FCSTD DOCUMENT  (FreeCAD 1.1R38827 (Git))
Label: composit_stand3_basement_assembly
License: All rights reserved
LicenseURL: http://en.wikipedia.org/wiki/All_rights_reserved
objects: App::Link×11, PartDesign::CoordinateSystem×5, App::DocumentObjectGroup×3, App::FeaturePython×1, Spreadsheet::Sheet×1, App::Part×1
note: 5 computed .brp shape members not serialized (recipe doc carries the construction recipe); baked Part::Feature solids carry a one-line shape summary decoded from their .brp
EXTERNAL_REF file=composit_stand3_basement_bottom_model.FCStd obj=Local_CS
EXTERNAL_REF file=composit_stand3_basement_bottom_model.FCStd obj=Body
EXTERNAL_REF file=composit_stand3_basement_amplifier_model.FCStd obj=Local_CS
EXTERNAL_REF file=composit_stand3_basement_bottom_PP_model.FCStd obj=Local_CS001
EXTERNAL_REF file=composit_stand3_basement_amplifier_model.FCStd obj=Body
EXTERNAL_REF file=../bearing_d100.FCStd obj=Local_CS001
EXTERNAL_REF file=composit_stand3_basement_bearing_holder_model.FCStd obj=Local_CS002
EXTERNAL_REF file=composit_stand3_basement_bearing_holder_model.FCStd obj=Body
EXTERNAL_REF file=composit_stand3_basement_amplifier_bearing_holder_model.FCStd obj=Local_CS001
EXTERNAL_REF file=composit_stand3_basement_bearing_holder_model.FCStd obj=Local_CS
EXTERNAL_REF file=composit_stand3_basement_amplifier_bearing_holder_model.FCStd obj=Body
EXTERNAL_REF file=composit_stand3_basement_amplifier_bearing_holder_model.FCStd obj=Local_CS
EXTERNAL_REF file=composit_stand3_basement_top_model.FCStd obj=Local_CS
EXTERNAL_REF file=composit_stand3_basement_top_model.FCStd obj=Body
EXTERNAL_REF file=composit_stand3_basement_top_model.FCStd obj=Local_CS002
EXTERNAL_REF file=../jamb_corner.FCStd obj=Local_CS
EXTERNAL_REF file=../jamb_corner.FCStd obj=Body
EXTERNAL_REF file=composit_stand3_basement_bottom_model.FCStd obj=Local_CS002
EXTERNAL_REF file=../prima_jamb.FCStd obj=Local_CS
EXTERNAL_REF file=../prima_jamb.FCStd obj=Body
EXTERNAL_REF file=composit_stand3_basement_top_PP_model.FCStd obj=Local_CS
EXTERNAL_REF file=composit_stand3_basement_top_model.FCStd obj=Local_CS001
EXTERNAL_REF file=composit_stand3_basement_top_PP_model.FCStd obj=Body
EXTERNAL_REF file=composit_stand3_basement_top_PP_model.FCStd obj=Local_CS001
EXTERNAL_REF file=composit_stand3_basin_holder_model.FCStd obj=Local_CS
EXTERNAL_REF file=composit_stand3_basin_holder_model.FCStd obj=Body
EXTERNAL_REF file=composit_stand3_basement_bottom_PP_model.FCStd obj=Local_CS
EXTERNAL_REF file=composit_stand3_basement_bottom_model.FCStd obj=Local_CS001
EXTERNAL_REF file=composit_stand3_basement_bottom_PP_model.FCStd obj=Body
EXTERNAL_REF file=../bearing_d100.FCStd obj=Local_CS
EXTERNAL_REF file=composit_stand3_basement_amplifier_model.FCStd obj=Local_CS002
EXTERNAL_REF file=../bearing_d100.FCStd obj=Body
EXTERNAL_REF file=composit_stand3_basement_bottom_model.FCStd obj=Local_CS003

FEATURE [App::DocumentObjectGroup] Parts
FEATURE [PartDesign::CoordinateSystem] LCS_Origin
  AttacherType = Attacher::AttachEngine3D
  AttachmentSupport = -> [X_Axis]
  MapMode = 2
FEATURE [App::DocumentObjectGroup] Constraints
FEATURE [App::FeaturePython] Variables  # WARN: FeaturePython — macro-defined, semantics opaque (R4)
  Type = App::PropertyContainer
FEATURE [App::DocumentObjectGroup] Configurations
FEATURE [App::Link] bottom
  AttachedBy = #Local_CS
  AttachedTo = Parent Assembly#LCS_Origin
  LinkedObject = -> <external composit_stand3_basement_bottom_model.FCStd>#Body
  SolverId = Asm4EE
  expr: Placement = LCS_Origin.Placement * AttachmentOffset * composit_stand3_basement_bottom_model#Local_CS.Placement ^ -1
FEATURE [App::Link] amplifier
  AttachedBy = #Local_CS
  AttachedTo = bottom_PP#Local_CS001
  LinkPlacement = pos=(0,0,21) rot=(0,0,1;0rad)
  LinkedObject = -> <external composit_stand3_basement_amplifier_model.FCStd>#Body
  Placement = pos=(0,0,21) rot=(0,0,1;0rad)
  SolverId = Asm4EE
  expr: Placement = bottom_PP.Placement * composit_stand3_basement_bottom_PP_model#Local_CS001.Placement * AttachmentOffset * composit_stand3_basement_amplifier_model#Local_CS.Placement ^ -1
FEATURE [App::Link] bearing_holder
  AttachedBy = #Local_CS002
  AttachedTo = bearing_d100#Local_CS001
  AttachmentOffset = pos=(0,0,0) rot=(1,0,0;3.14159rad)
  LinkPlacement = pos=(0,2e-15,72) rot=(1,0,0;3.14159rad)
  LinkedObject = -> <external composit_stand3_basement_bearing_holder_model.FCStd>#Body
  Placement = pos=(0,2e-15,72) rot=(1,0,0;3.14159rad)
  SolverId = Asm4EE
  expr: Placement = bearing_d100.Placement * bearing_d100#Local_CS001.Placement * AttachmentOffset * composit_stand3_basement_bearing_holder_model#Local_CS002.Placement ^ -1
FEATURE [App::Link] amplifier_bearing_holder
  AttachedBy = #Local_CS001
  AttachedTo = bearing_holder#Local_CS
  LinkPlacement = pos=(0,4.2e-15,90) rot=(1,0,0;3.14159rad)
  LinkedObject = -> <external composit_stand3_basement_amplifier_bearing_holder_model.FCStd>#Body
  Placement = pos=(0,4.2e-15,90) rot=(1,0,0;3.14159rad)
  SolverId = Asm4EE
  expr: Placement = bearing_holder.Placement * composit_stand3_basement_bearing_holder_model#Local_CS.Placement * AttachmentOffset * composit_stand3_basement_amplifier_bearing_holder_model#Local_CS001.Placement ^ -1
FEATURE [App::Link] top
  AttachedBy = #Local_CS
  AttachedTo = amplifier_bearing_holder#Local_CS
  AttachmentOffset = pos=(0,0,0) rot=(1,0,0;3.14159rad)
  LinkPlacement = pos=(0,4.2e-15,90) rot=(0,0,1;0rad)
  LinkedObject = -> <external composit_stand3_basement_top_model.FCStd>#Body
  Placement = pos=(0,4.2e-15,90) rot=(0,0,1;0rad)
  SolverId = Asm4EE
  expr: Placement = amplifier_bearing_holder.Placement * composit_stand3_basement_amplifier_bearing_holder_model#Local_CS.Placement * AttachmentOffset * composit_stand3_basement_top_model#Local_CS.Placement ^ -1
FEATURE [App::Link] jamb_corner
  AttachedBy = #Local_CS
  AttachedTo = top#Local_CS002
  LinkPlacement = pos=(215,-2.1,90) rot=(-0.57735,-0.57735,0.57735;2.0944rad)
  LinkedObject = -> <external ../jamb_corner.FCStd>#Body
  Placement = pos=(215,-2.1,90) rot=(-0.57735,-0.57735,0.57735;2.0944rad)
  SolverId = Asm4EE
  expr: Placement = top.Placement * composit_stand3_basement_top_model#Local_CS002.Placement * AttachmentOffset * jamb_corner#Local_CS.Placement ^ -1
FEATURE [App::Link] prima_jamb
  AttachedBy = #Local_CS
  AttachedTo = bottom#Local_CS002
  LinkPlacement = pos=(215,0,21) rot=(0,0,1;0rad)
  LinkedObject = -> <external ../prima_jamb.FCStd>#Body
  Placement = pos=(215,0,21) rot=(0,0,1;0rad)
  SolverId = Asm4EE
  expr: Placement = bottom.Placement * composit_stand3_basement_bottom_model#Local_CS002.Placement * AttachmentOffset * prima_jamb#Local_CS.Placement ^ -1
FEATURE [App::Link] top_PP
  AttachedBy = #Local_CS
  AttachedTo = top#Local_CS001
  LinkPlacement = pos=(0,8.6e-15,108) rot=(0,0,1;0rad)
  LinkedObject = -> <external composit_stand3_basement_top_PP_model.FCStd>#Body
  Placement = pos=(0,8.6e-15,108) rot=(0,0,1;0rad)
  SolverId = Asm4EE
  expr: Placement = top.Placement * composit_stand3_basement_top_model#Local_CS001.Placement * AttachmentOffset * composit_stand3_basement_top_PP_model#Local_CS.Placement ^ -1
FEATURE [App::Link] basin_holder
  AttachedBy = #Local_CS
  AttachedTo = top_PP#Local_CS001
  LinkPlacement = pos=(0,9.3e-15,111) rot=(0,0,1;0rad)
  LinkedObject = -> <external composit_stand3_basin_holder_model.FCStd>#Body
  Placement = pos=(0,9.3e-15,111) rot=(0,0,1;0rad)
  SolverId = Asm4EE
  expr: Placement = top_PP.Placement * composit_stand3_basement_top_PP_model#Local_CS001.Placement * AttachmentOffset * composit_stand3_basin_holder_model#Local_CS.Placement ^ -1
FEATURE [App::Link] bottom_PP
  AttachedBy = #Local_CS
  AttachedTo = bottom#Local_CS001
  LinkPlacement = pos=(0,0,18) rot=(0,0,1;0rad)
  LinkedObject = -> <external composit_stand3_basement_bottom_PP_model.FCStd>#Body
  Placement = pos=(0,0,18) rot=(0,0,1;0rad)
  SolverId = Asm4EE
  expr: Placement = bottom.Placement * composit_stand3_basement_bottom_model#Local_CS001.Placement * AttachmentOffset * composit_stand3_basement_bottom_PP_model#Local_CS.Placement ^ -1
FEATURE [PartDesign::CoordinateSystem] top_LCS
  AttacherType = Attacher::AttachEngine3D
  AttachmentSupport = -> [top_PP]
  Placement = pos=(0,0,111) rot=(0,0,1;0rad)
FEATURE [App::Link] bearing_d100
  AttachedBy = #Local_CS
  AttachedTo = amplifier#Local_CS002
  LinkPlacement = pos=(0,0,37) rot=(0,0,1;0rad)
  LinkedObject = -> <external ../bearing_d100.FCStd>#Body
  Placement = pos=(0,0,37) rot=(0,0,1;0rad)
  SolverId = Asm4EE
  expr: Placement = amplifier.Placement * composit_stand3_basement_amplifier_model#Local_CS002.Placement * AttachmentOffset * bearing_d100#Local_CS.Placement ^ -1
FEATURE [Spreadsheet::Sheet] Spreadsheet  label="Properties"
  cells = B2(total_height)==111 mm
FEATURE [PartDesign::CoordinateSystem] bar1_LCS
  AttacherType = Attacher::AttachEngine3D
  AttachmentOffset = pos=(383.5,0,21) rot=(0,0,1;3.14159rad)
  AttachmentSupport = -> [LCS_Origin]
  MapMode = 5
  Placement = pos=(383.5,0,21) rot=(0,0,1;3.14159rad)
  expr: AttachmentOffset = <<bottom>>.Placement * <<composit_stand3_basement_bottom_model>>#<<bar_LCS>>.Placement
FEATURE [PartDesign::CoordinateSystem] bar2_LCS
  AttacherType = Attacher::AttachEngine3D
  AttachmentOffset = pos=(-191.75,332.121,21) rot=(0,0,1;5.23599rad)
  AttachmentSupport = -> [LCS_Origin]
  MapMode = 5
  Placement = pos=(-191.75,332.121,21) rot=(0,0,1;5.23599rad)
  expr: AttachmentOffset = placement(vector(0; 0; 0); rotation(120 deg; 0; 0)) * <<bottom>>.Placement * <<composit_stand3_basement_bottom_model>>#<<bar_LCS>>.Placement
FEATURE [PartDesign::CoordinateSystem] bar3_LCS
  AttacherType = Attacher::AttachEngine3D
  AttachmentOffset = pos=(-191.75,-332.121,21) rot=(0,0,-1;5.23599rad)
  AttachmentSupport = -> [LCS_Origin]
  MapMode = 5
  Placement = pos=(-191.75,-332.121,21) rot=(0,0,-1;5.23599rad)
  expr: AttachmentOffset = placement(vector(0; 0; 0); rotation(240 deg; 0; 0)) * <<bottom>>.Placement * <<composit_stand3_basement_bottom_model>>#<<bar_LCS>>.Placement
FEATURE [App::Part] Assembly  label="basement_Assembly"
  AssemblyType = Part::Link
  Group = -> [LCS_Origin,Constraints,Variables,Configurations,bottom,amplifier,bearing_holder,amplifier_bearing_holder,top,jamb_corner,prima_jamb,top_PP,basin_holder,bottom_PP,top_LCS,bearing_d100,bar1_LCS,bar2_LCS,bar3_LCS]
  Origin = -> Origin
  Type = Assembly

RESOLVED EXTERNAL PARTS (link-assembly join: the EXTERNAL_REF files above that resolve inside this repo's crawl, each included once):
---- part ../bearing_d100.FCStd = doc fcstd_fc5883dd0358 ----
FCSTD DOCUMENT  (FreeCAD 1.1R38827 (Git))
Label: bearing_d100
License: All rights reserved
LicenseURL: http://en.wikipedia.org/wiki/All_rights_reserved
objects: PartDesign::CoordinateSystem×2, Sketcher::SketchObject×1, PartDesign::SubShapeBinder×1, PartDesign::Revolution×1, PartDesign::Body×1
note: 9 computed .brp shape members not serialized (recipe doc carries the construction recipe); baked Part::Feature solids carry a one-line shape summary decoded from their .brp

FEATURE [Sketcher::SketchObject] Sketch  label="main_Sketch"
  ArcFitTolerance = 0
  FullyConstrained = true
  MakeInternals = false
  Placement = pos=(0,0,0) rot=(1,0,0;1.5708rad)
  sketch-geometry (4):
    g0: LineSegment StartX=37.5 StartY=0 StartZ=0 EndX=50 EndY=0 EndZ=0
    g1: LineSegment StartX=50 StartY=0 StartZ=0 EndX=50 EndY=19 EndZ=0
    g2: LineSegment StartX=50 StartY=19 StartZ=0 EndX=37.5 EndY=19 EndZ=0
    g3: LineSegment StartX=37.5 StartY=19 StartZ=0 EndX=37.5 EndY=0 EndZ=0
  constraints (12):
    c: Coincident(g0,g1)
    c: Coincident(g1,g2)
    c: Coincident(g2,g3)
    c: Coincident(g3,g0)
    c: Horizontal(g0)
    c: Horizontal(g2)
    c: Vertical(g1)
    c: Vertical(g3)
    c: PointOnObject(g0,g-1)
    c: DistanceX(g0) = 37.5  'min_r'
    c: DistanceX(g0) = 50  'max_r'
    c: DistanceY(g3,g3) = 19  'height'
FEATURE [PartDesign::SubShapeBinder] Binder
  BindCopyOnChange = 0
  BindMode = 0
  ClaimChildren = true
  Context = -> Body [Binder.]
  Fuse = false
  MakeFace = true
  OffsetFill = false
  OffsetIntersection = false
  OffsetJoinType = 0
  OffsetOpenResult = false
  PartialLoad = false
  Placement = pos=(0,0,0) rot=(1,0,0;1.5708rad)
  Relative = false
  Support = -> [Sketch]
  _Version = 2
  expr: Placement = Support[0][0].Placement
FEATURE [PartDesign::Revolution] Revolution
  Angle = 360
  Angle2 = 60
  Axis = (1e-16,1e-16,1)
  Base = (0,0,0)
  Placement = pos=(0,0,0) rot=(1,0,0;1.5708rad)
  Profile = -> Binder [Face1]
  ReferenceAxis = -> Z_Axis
  Reversed = true
  Suppressed = false
  Type = 0
FEATURE [PartDesign::CoordinateSystem] Local_CS  label="bottom_LCS"
  AttacherType = Attacher::AttachEngine3D
  AttachmentSupport = -> [XY_Plane]
  MapMode = 5
FEATURE [PartDesign::CoordinateSystem] Local_CS001  label="top_LCS"
  AttacherType = Attacher::AttachEngine3D
  AttachmentOffset = pos=(0,0,19) rot=(0,0,1;0rad)
  AttachmentSupport = -> [XY_Plane]
  MapMode = 5
  Placement = pos=(0,0,19) rot=(0,0,1;0rad)
  expr: .AttachmentOffset.Base.z = <<main_Sketch>>.Constraints.height
FEATURE [PartDesign::Body] Body  label="bearing_d100"
  AllowCompound = false
  Group = -> [Binder,Revolution,Local_CS,Local_CS001]
  Origin = -> Origin
  Tip = -> Revolution
---- part ../jamb_corner.FCStd = doc fcstd_c531c7f2f68e ----
FCSTD DOCUMENT  (FreeCAD 1.1R38827 (Git))
Label: jamb_corner
License: All rights reserved
LicenseURL: http://en.wikipedia.org/wiki/All_rights_reserved
objects: Part::FeaturePython×5, PartDesign::Body×2, Sketcher::SketchObject×1, PartDesign::FeaturePython×1, Part::Cylinder×1, Part::MultiFuse×1, PartDesign::Boolean×1, PartDesign::CoordinateSystem×1
note: 16 computed .brp shape members not serialized (recipe doc carries the construction recipe); baked Part::Feature solids carry a one-line shape summary decoded from their .brp

FEATURE [Sketcher::SketchObject] Sketch
  ArcFitTolerance = 0
  FullyConstrained = true
  MakeInternals = false
  sketch-geometry (2):
    g0: LineSegment StartX=0 StartY=61.5 StartZ=0 EndX=0 EndY=0 EndZ=0
    g1: LineSegment StartX=0 StartY=0 StartZ=0 EndX=102 EndY=0 EndZ=0
  constraints (6):
    c: PointOnObject(g0,g-2)
    c: Coincident(g0,g-1)
    c: Coincident(g0,g1)
    c: PointOnObject(g1,g-1)
    c: DistanceX(g1) = 102
    c: DistanceY(g0) = 61.5
FEATURE [Part::FeaturePython] Placment  # WARN: FeaturePython — macro-defined, semantics opaque (R4)
  AttacherType = Attacher::AttachEngine3D
  ExposePlacement = true
  MarkerShape = 1
  MarkerSize = 50
  NumElements = 1
  Placement = pos=(43.5,0,0) rot=(1,0,0;0rad)
  Type = lattice2AttachablePlacement.AttachablePlacement
  isLattice = 1
FEATURE [Part::FeaturePython] Placment001  # WARN: FeaturePython — macro-defined, semantics opaque (R4)
  AttacherType = Attacher::AttachEngine3D
  ExposePlacement = true
  MarkerShape = 1
  MarkerSize = 50
  NumElements = 1
  Placement = pos=(68.5,0,0) rot=(1,0,0;0rad)
  Type = lattice2AttachablePlacement.AttachablePlacement
  isLattice = 1
FEATURE [Part::FeaturePython] Placment002  # WARN: FeaturePython — macro-defined, semantics opaque (R4)
  AttacherType = Attacher::AttachEngine3D
  ExposePlacement = true
  MarkerShape = 1
  MarkerSize = 50
  NumElements = 1
  Placement = pos=(91,0,0) rot=(1,0,0;0rad)
  Type = lattice2AttachablePlacement.AttachablePlacement
  isLattice = 1
FEATURE [PartDesign::FeaturePython] BaseBend  # WARN: FeaturePython — macro-defined, semantics opaque (R4)
  BendSide = 1
  BendSketch = -> Sketch
  MidPlane = true
  Reverse = false
  Suppressed = false
  length = 20
  radius = 6
  thickness = 4.3
FEATURE [Part::Cylinder] Cylinder
  Angle = 360
  AttacherType = Attacher::AttachEngine3D
  FirstAngle = 0
  Height = 10
  Placement = pos=(0,0,0) rot=(1,0,0;3.14159rad)
  Radius = 2
  SecondAngle = 0
FEATURE [Part::FeaturePython] Join  label="holes_hor"  # WARN: FeaturePython — macro-defined, semantics opaque (R4)
  ExposePlacement = false
  Interleave = false
  Links = -> [Placment,Placment001,Placment002]
  MarkerShape = 1
  MarkerSize = 0
  NumElements = 3
  Placement = pos=(0,0,0) rot=(1,0,0;1.5708rad)
  Type = lattice2JoinArrays.JoinArrays
  isLattice = 1
FEATURE [Part::FeaturePython] Populate  label="Populate holes_hor with Cylinder"  # WARN: FeaturePython — macro-defined, semantics opaque (R4)
  Copying = 0
  ExposePlacement = false
  MarkerShape = 1
  MarkerSize = 0
  NumElements = 0
  Object = -> Cylinder
  OutputCompounding = 1
  PlacementsTo = -> Join
  Referencing = 0
  Type = lattice2PopulateCopies.LatticePopulateCopies
  isLattice = 0
FEATURE [PartDesign::Body] Body001
  AllowCompound = false
  Origin = -> Origin001
FEATURE [Part::MultiFuse] Fusion
  Shapes = -> [Populate]
FEATURE [PartDesign::Boolean] Boolean
  BaseFeature = -> BaseBend
  Group = -> [Fusion]
  Suppressed = false
  Type = 1
  UsePlacement = true
FEATURE [PartDesign::CoordinateSystem] Local_CS  label="base_LCS"
  AttacherType = Attacher::AttachEngine3D
  AttachmentSupport = -> [YZ_Plane]
  MapMode = 5
  Placement = pos=(0,0,0) rot=(0.57735,0.57735,0.57735;2.0944rad)
FEATURE [PartDesign::Body] Body  label="jamb_corner"
  AllowCompound = false
  Group = -> [BaseBend,Boolean,Local_CS]
  Origin = -> Origin
  Tip = -> Boolean
---- part ../prima_jamb.FCStd = doc fcstd_baa8a8553cea ----
FCSTD DOCUMENT  (FreeCAD 1.1R38827 (Git))
Label: prima_jamb
License: All rights reserved
LicenseURL: http://en.wikipedia.org/wiki/All_rights_reserved
objects: Sketcher::SketchObject×1, PartDesign::Revolution×1, Part::Cylinder×1, Part::Compound×1, PartDesign::Boolean×1, PartDesign::CoordinateSystem×1, PartDesign::Body×1
note: 11 computed .brp shape members not serialized (recipe doc carries the construction recipe); baked Part::Feature solids carry a one-line shape summary decoded from their .brp

FEATURE [Sketcher::SketchObject] Sketch
  ArcFitTolerance = 0
  AttachmentSupport = -> [XZ_Plane]
  FullyConstrained = true
  MakeInternals = false
  MapMode = 5
  Placement = pos=(0,0,0) rot=(1,0,0;1.5708rad)
  sketch-geometry (6):
    g0: LineSegment StartX=0 StartY=0 StartZ=0 EndX=20.75 EndY=0 EndZ=0
    g1: LineSegment StartX=20.75 StartY=0 StartZ=0 EndX=20.75 EndY=48.0542 EndZ=0
    g2: ArcOfCircle CenterX=18.1 CenterY=40.4 CenterZ=0 NormalX=0 NormalY=0 NormalZ=1 AngleXU=0 Radius=8.1 StartAngle=1.2375 EndAngle=3.14159
    g3: LineSegment StartX=0 StartY=0 StartZ=0 EndX=0 EndY=40.4 EndZ=0
    g4: LineSegment StartX=0 StartY=40.4 StartZ=0 EndX=10 EndY=40.4 EndZ=0
    g5: LineSegment [constr] StartX=0 StartY=48.5 StartZ=0 EndX=18.1 EndY=48.5 EndZ=0
  constraints (18):
    c: Coincident(g-1,g0)
    c: PointOnObject(g0,g-1)
    c: Coincident(g0,g1)
    c: Vertical(g1)
    c: Coincident(g0,g3)
    c: PointOnObject(g3,g-2)
    c: Coincident(g3,g4)
    c: Coincident(g4,g2)
    c: Horizontal(g4)
    c: DistanceX(g0) = 20.75
    c: Perpendicular(g2,g4)
    c: DistanceX(g2) = 10
    c: Tangent(g5,g2) = 1.5708
    c: Horizontal(g5)
    c: PointOnObject(g5,g-2)
    c: DistanceY(g3,g5) = 8.1
    c: Coincident(g1,g2)
    c: DistanceY(g5) = 48.5
FEATURE [PartDesign::Revolution] Revolution
  Angle = 360
  Angle2 = 60
  Axis = (0,2e-16,1)
  Base = (0,0,0)
  Placement = pos=(0,0,0) rot=(1,0,0;1.5708rad)
  Profile = -> Sketch
  ReferenceAxis = -> Sketch [V_Axis]
  Reversed = true
  Suppressed = false
  Type = 0
FEATURE [Part::Cylinder] Cylinder
  Angle = 360
  AttacherType = Attacher::AttachEngine3D
  FirstAngle = 0
  Height = 50
  Radius = 3.5
  SecondAngle = 0
FEATURE [Part::Compound] Compound
  Links = -> [Cylinder]
FEATURE [PartDesign::Boolean] Boolean
  BaseFeature = -> Revolution
  Group = -> [Compound]
  Suppressed = false
  Type = 1
  UsePlacement = true
FEATURE [PartDesign::CoordinateSystem] Local_CS
  AttacherType = Attacher::AttachEngine3D
  AttachmentSupport = -> [XY_Plane]
  MapMode = 5
FEATURE [PartDesign::Body] Body  label="prima_jamb"
  AllowCompound = false
  Group = -> [Sketch,Revolution,Boolean,Local_CS]
  Origin = -> Origin
  Tip = -> Boolean
---- part composit_stand3_basement_amplifier_bearing_holder_model.FCStd = doc fcstd_344d85539f5e ----
FCSTD DOCUMENT  (FreeCAD 1.1R38827 (Git))
Label: composit_stand3_basement_amplifier_bearing_holder_model
License: All rights reserved
LicenseURL: http://en.wikipedia.org/wiki/All_rights_reserved
objects: Part::FeaturePython×5, PartDesign::SubShapeBinder×2, PartDesign::Pad×2, App::Link×2, PartDesign::Body×2, PartDesign::CoordinateSystem×2, Part::Mirroring×1, Part::Compound×1, Part::Cylinder×1, Sketcher::SketchObject×1, Part::MultiFuse×1, PartDesign::Boolean×1
note: 25 computed .brp shape members not serialized (recipe doc carries the construction recipe); baked Part::Feature solids carry a one-line shape summary decoded from their .brp
EXTERNAL_REF file=composit_stand3_basement_amplifier_main.FCStd obj=Sketch
EXTERNAL_REF file=composit_stand3_basement_amplifier_main.FCStd obj=Join001
EXTERNAL_REF file=composit_stand3_basement_amplifier_main.FCStd obj=Cylinder

FEATURE [PartDesign::SubShapeBinder] Binder
  BindCopyOnChange = 0
  BindMode = 0
  ClaimChildren = true
  Fuse = false
  MakeFace = true
  OffsetFill = false
  OffsetIntersection = false
  OffsetJoinType = 0
  OffsetOpenResult = false
  PartialLoad = false
  Relative = true
  Support = -> [<external composit_stand3_basement_amplifier_main.FCStd>#Sketch]
  _Version = 2
FEATURE [Part::Mirroring] Part__Mirroring  label="Binder (Mirror #1)"
  Base = (0,0,0)
  Normal = (0,1,0)
  Source = -> Binder
FEATURE [Part::FeaturePython] PolarArray  # WARN: FeaturePython — macro-defined, semantics opaque (R4)
  Alignment = 0
  AttacherType = Attacher::AttachEngine3D
  CellStart = A1
  Count = 3
  DistributionLaw = 0
  EndInclusive = false
  ExposePlacement = false
  FlipX = false
  FlipZ = false
  GeneratorMode = 0
  MarkerShape = 1
  MarkerSize = 0
  NumElements = 3
  OrientMode = 2
  Radius = 100
  Reverse = false
  SpanEnd = 360
  SpanStart = 0
  Step = 120
  Type = lattice2PolarArray2.PolarArray
  UseArcRadius = false
  UseArcRange = 0
  VSGVersion = 1
  Values = 0.0 | 120.0 | 240.0
  ValuesSource = 2
  isLattice = 1
FEATURE [Part::Compound] Compound
  Links = -> [Binder,Part__Mirroring]
FEATURE [Part::FeaturePython] Populate  label="Populate PolarArray with Compound"  # WARN: FeaturePython — macro-defined, semantics opaque (R4)
  Copying = 0
  ExposePlacement = false
  MarkerShape = 1
  MarkerSize = 0
  NumElements = 0
  Object = -> Compound
  OutputCompounding = 1
  PlacementsTo = -> PolarArray
  Referencing = 1
  Type = lattice2PopulateCopies.LatticePopulateCopies
  isLattice = 0
FEATURE [Part::FeaturePython] Connect  # WARN: FeaturePython — macro-defined, semantics opaque (R4)
  Objects = -> [Populate]
  Tolerance = 0
FEATURE [PartDesign::SubShapeBinder] Binder001
  BindCopyOnChange = 0
  BindMode = 0
  ClaimChildren = true
  Context = -> Body [Binder001.]
  Fuse = false
  MakeFace = false
  OffsetFill = false
  OffsetIntersection = false
  OffsetJoinType = 0
  OffsetOpenResult = false
  PartialLoad = false
  Relative = true
  Support = -> [Connect]
  _Version = 2
FEATURE [PartDesign::Pad] Pad
  Direction = (0,0,1)
  Length = 18
  Length2 = 10
  Profile = -> Binder001
  Refine = true
  Suppressed = false
  Type = 0
FEATURE [App::Link] Link  label="Populate PolarArray with Join"
  LinkedObject = -> <external composit_stand3_basement_amplifier_main.FCStd>#Join001
FEATURE [Part::Cylinder] Cylinder  label="hole_5,2_mm"
  Angle = 360
  AttacherType = Attacher::AttachEngine3D
  FirstAngle = 0
  Height = 18
  Radius = 2.6
  SecondAngle = 0
FEATURE [Part::FeaturePython] Join  label="holes_placements"  # WARN: FeaturePython — macro-defined, semantics opaque (R4)
  ExposePlacement = false
  Interleave = false
  Links = -> [Link]
  MarkerShape = 1
  MarkerSize = 0
  NumElements = 14
  Type = lattice2JoinArrays.JoinArrays
  isLattice = 1
FEATURE [Part::FeaturePython] Populate001  label="Populate Populate PolarArray with Join with hole_5_mm"  # WARN: FeaturePython — macro-defined, semantics opaque (R4)
  Copying = 0
  ExposePlacement = false
  MarkerShape = 1
  MarkerSize = 0
  NumElements = 0
  Object = -> Cylinder
  OutputCompounding = 1
  PlacementsTo = -> Join
  Referencing = 0
  Type = lattice2PopulateCopies.LatticePopulateCopies
  isLattice = 0
FEATURE [App::Link] Link003  label="axis_bolt"
  LinkedObject = -> <external composit_stand3_basement_amplifier_main.FCStd>#Cylinder
FEATURE [Sketcher::SketchObject] Sketch
  ArcFitTolerance = 0
  AttachmentSupport = -> [XY_Plane002]
  FullyConstrained = true
  MakeInternals = false
  MapMode = 5
  sketch-geometry (7):
    g0: LineSegment StartX=11.0274 StartY=0 StartZ=0 EndX=5.5137 EndY=9.55 EndZ=0
    g1: LineSegment StartX=5.5137 StartY=9.55 StartZ=0 EndX=-5.5137 EndY=9.55 EndZ=0
    g2: LineSegment StartX=-5.5137 StartY=9.55 StartZ=0 EndX=-11.0274 EndY=0 EndZ=0
    g3: LineSegment StartX=-11.0274 StartY=1e-16 StartZ=0 EndX=-5.5137 EndY=-9.55 EndZ=0
    g4: LineSegment StartX=-5.5137 StartY=-9.55 StartZ=0 EndX=5.5137 EndY=-9.55 EndZ=0
    g5: LineSegment StartX=5.5137 StartY=-9.55 StartZ=0 EndX=11.0274 EndY=0 EndZ=0
    g6: Circle [constr] CenterX=0 CenterY=0 CenterZ=0 NormalX=0 NormalY=0 NormalZ=1 AngleXU=0 Radius=11.0274
  constraints (16):
    c: Coincident(g0,g1)
    c: Coincident(g1,g2)
    c: Coincident(g2,g3)
    c: Coincident(g3,g4)
    c: Coincident(g4,g5)
    c: Coincident(g5,g0)
    c: Equal(g0, g1-g5) x5
    c: PointOnObject(g0,g6)
    c: PointOnObject(g1,g6)
    c: PointOnObject(g2,g6)
    c: PointOnObject(g3,g6)
    c: PointOnObject(g4,g6)
    c: PointOnObject(g5,g6)
    c: Coincident(g6,g-1)
    c: PointOnObject(g5,g-1)
    c: DistanceY(g4,g0) = 19.1
FEATURE [PartDesign::Pad] Pad001
  Direction = (0,0,1)
  Length = 7.4
  Length2 = 10
  Profile = -> Sketch
  ReferenceAxis = -> Sketch [N_Axis]
  Suppressed = false
  Type = 0
FEATURE [PartDesign::Body] Body002  label="Body003"
  AllowCompound = false
  Group = -> [Sketch,Pad001]
  Origin = -> Origin002
  Tip = -> Pad001
FEATURE [Part::MultiFuse] Fusion
  Shapes = -> [Populate001,Link003,Body002]
FEATURE [PartDesign::Boolean] Boolean
  BaseFeature = -> Pad
  Group = -> [Fusion]
  Suppressed = false
  Type = 1
  UsePlacement = true
FEATURE [PartDesign::CoordinateSystem] Local_CS  label="bottom_LCS"
  AttacherType = Attacher::AttachEngine3D
  AttachmentSupport = -> [XY_Plane]
  MapMode = 5
FEATURE [PartDesign::CoordinateSystem] Local_CS001  label="top_LCS"
  AttacherType = Attacher::AttachEngine3D
  AttachmentOffset = pos=(0,0,18) rot=(0,0,1;0rad)
  AttachmentSupport = -> [XY_Plane]
  MapMode = 5
  Placement = pos=(0,0,18) rot=(0,0,1;0rad)
FEATURE [PartDesign::Body] Body  label="amplifier_bearing_holder"
  AllowCompound = false
  Group = -> [Binder001,Pad,Boolean,Local_CS,Local_CS001]
  Origin = -> Origin
  Tip = -> Boolean
---- part composit_stand3_basement_amplifier_model.FCStd = doc fcstd_fba40b1622f7 ----
FCSTD DOCUMENT  (FreeCAD 1.1R38827 (Git))
Label: composit_stand3_basement_amplifier_model
License: All rights reserved
LicenseURL: http://en.wikipedia.org/wiki/All_rights_reserved
objects: Part::FeaturePython×6, App::Link×5, PartDesign::CoordinateSystem×3, PartDesign::SubShapeBinder×2, Part::Mirroring×1, Part::Compound×1, PartDesign::Pad×1, Part::Cylinder×1, Part::MultiFuse×1, PartDesign::Boolean×1, PartDesign::Body×1
note: 21 computed .brp shape members not serialized (recipe doc carries the construction recipe); baked Part::Feature solids carry a one-line shape summary decoded from their .brp
EXTERNAL_REF file=composit_stand3_basement_amplifier_main.FCStd obj=Sketch
EXTERNAL_REF file=composit_stand3_basement_amplifier_main.FCStd obj=Join001
EXTERNAL_REF file=composit_stand3_basement_amplifier_main.FCStd obj=Cylinder
EXTERNAL_REF file=composit_stand3_basement_bearing_holder_main.FCStd obj=Placment
EXTERNAL_REF file=../bearing_d100.FCStd obj=Body
EXTERNAL_REF file=composit_stand3_basement_amplifier_main.FCStd obj=Body

FEATURE [PartDesign::SubShapeBinder] Binder
  BindCopyOnChange = 0
  BindMode = 0
  ClaimChildren = false
  Fuse = false
  MakeFace = true
  OffsetFill = false
  OffsetIntersection = false
  OffsetJoinType = 0
  OffsetOpenResult = false
  PartialLoad = false
  Relative = true
  Support = -> [<external composit_stand3_basement_amplifier_main.FCStd>#Sketch]
  _Version = 2
FEATURE [Part::Mirroring] Part__Mirroring  label="Binder (Mirror #1)"
  Base = (0,0,0)
  Normal = (0,1,0)
  Source = -> Binder
FEATURE [Part::FeaturePython] PolarArray  # WARN: FeaturePython — macro-defined, semantics opaque (R4)
  Alignment = 0
  AttacherType = Attacher::AttachEngine3D
  CellStart = A1
  Count = 3
  DistributionLaw = 0
  EndInclusive = false
  ExposePlacement = false
  FlipX = false
  FlipZ = false
  GeneratorMode = 0
  MarkerShape = 1
  MarkerSize = 0
  NumElements = 3
  OrientMode = 2
  Radius = 100
  Reverse = false
  SpanEnd = 360
  SpanStart = 0
  Step = 120
  Type = lattice2PolarArray2.PolarArray
  UseArcRadius = false
  UseArcRange = 0
  VSGVersion = 1
  Values = 0.0 | 120.0 | 240.0
  ValuesSource = 2
  isLattice = 1
FEATURE [Part::Compound] Compound
  Links = -> [Binder,Part__Mirroring]
FEATURE [Part::FeaturePython] Populate  label="Populate PolarArray with Compound"  # WARN: FeaturePython — macro-defined, semantics opaque (R4)
  Copying = 0
  ExposePlacement = false
  MarkerShape = 1
  MarkerSize = 0
  NumElements = 0
  Object = -> Compound
  OutputCompounding = 1
  PlacementsTo = -> PolarArray
  Referencing = 1
  Type = lattice2PopulateCopies.LatticePopulateCopies
  isLattice = 0
FEATURE [Part::FeaturePython] Connect  # WARN: FeaturePython — macro-defined, semantics opaque (R4)
  Objects = -> [Populate]
  Tolerance = 0
FEATURE [PartDesign::SubShapeBinder] Binder001
  BindCopyOnChange = 0
  BindMode = 0
  ClaimChildren = true
  Context = -> Body [Binder001.]
  Fuse = false
  MakeFace = false
  OffsetFill = false
  OffsetIntersection = false
  OffsetJoinType = 0
  OffsetOpenResult = false
  PartialLoad = false
  Relative = true
  Support = -> [Connect]
  _Version = 2
FEATURE [PartDesign::Pad] Pad
  Direction = (0,0,1)
  Length = 18
  Length2 = 10
  Profile = -> Binder001
  Refine = true
  Suppressed = false
  Type = 0
FEATURE [App::Link] Link  label="Populate PolarArray with Join"
  LinkedObject = -> <external composit_stand3_basement_amplifier_main.FCStd>#Join001
FEATURE [Part::Cylinder] Cylinder  label="hole_5,2_mm"
  Angle = 360
  AttacherType = Attacher::AttachEngine3D
  FirstAngle = 0
  Height = 18
  Radius = 2.6
  SecondAngle = 0
FEATURE [Part::FeaturePython] Join  label="holes_placements"  # WARN: FeaturePython — macro-defined, semantics opaque (R4)
  ExposePlacement = false
  Interleave = false
  Links = -> [Link]
  MarkerShape = 1
  MarkerSize = 0
  NumElements = 14
  Type = lattice2JoinArrays.JoinArrays
  isLattice = 1
FEATURE [App::Link] Link001  label="axis_bolt"
  LinkedObject = -> <external composit_stand3_basement_amplifier_main.FCStd>#Cylinder
FEATURE [PartDesign::CoordinateSystem] Local_CS  label="bottom_LCS"
  AttacherType = Attacher::AttachEngine3D
  AttachmentSupport = -> [XY_Plane]
  MapMode = 5
FEATURE [PartDesign::CoordinateSystem] Local_CS001  label="top_LCS"
  AttacherType = Attacher::AttachEngine3D
  AttachmentOffset = pos=(0,0,18) rot=(0,0,1;0rad)
  AttachmentSupport = -> [XY_Plane]
  MapMode = 5
  Placement = pos=(0,0,18) rot=(0,0,1;0rad)
FEATURE [App::Link] Link002  label="bearing_placement"
  LinkTransform = true
  LinkedObject = -> <external composit_stand3_basement_bearing_holder_main.FCStd>#Placment
FEATURE [App::Link] Link003  label="Body"
  LinkedObject = -> <external ../bearing_d100.FCStd>#Body
FEATURE [Part::FeaturePython] Populate002  label="Populate bearing_placement with Body"  # WARN: FeaturePython — macro-defined, semantics opaque (R4)
  Copying = 0
  ExposePlacement = false
  MarkerShape = 1
  MarkerSize = 0
  NumElements = 0
  Object = -> Link003
  OutputCompounding = 2
  PlacementsTo = -> Link002
  Referencing = 0
  Type = lattice2PopulateCopies.LatticePopulateCopies
  isLattice = 0
FEATURE [PartDesign::CoordinateSystem] Local_CS002  label="bearing_LCS"
  AttacherType = Attacher::AttachEngine3D
  AttachmentOffset = pos=(0,0,16) rot=(0,0,1;0rad)
  AttachmentSupport = -> [XY_Plane]
  MapMode = 5
  Placement = pos=(0,0,16) rot=(0,0,1;0rad)
  expr: AttachmentOffset = <<bearing_placement>>.LinkedObject.Placement
FEATURE [App::Link] Link004  label="screw"
  LinkedObject = -> <external composit_stand3_basement_amplifier_main.FCStd>#Body
FEATURE [Part::FeaturePython] Populate001  label="Populate Populate PolarArray with Join with hole_5_mm"  # WARN: FeaturePython — macro-defined, semantics opaque (R4)
  Copying = 0
  ExposePlacement = false
  MarkerShape = 1
  MarkerSize = 0
  NumElements = 0
  Object = -> Link004
  OutputCompounding = 1
  PlacementsTo = -> Join
  Referencing = 0
  Type = lattice2PopulateCopies.LatticePopulateCopies
  isLattice = 0
FEATURE [Part::MultiFuse] Fusion
  Shapes = -> [Populate001,Link001,Populate002]
FEATURE [PartDesign::Boolean] Boolean
  BaseFeature = -> Pad
  Group = -> [Fusion]
  Suppressed = false
  Type = 1
  UsePlacement = true
FEATURE [PartDesign::Body] Body  label="amplifier"
  AllowCompound = false
  Group = -> [Binder001,Pad,Boolean,Local_CS,Local_CS001,Local_CS002]
  Origin = -> Origin
  Tip = -> Boolean
---- part composit_stand3_basement_bearing_holder_model.FCStd = doc fcstd_b06b4b549dd2 ----
FCSTD DOCUMENT  (FreeCAD 1.1R38827 (Git))
Label: composit_stand3_basement_bearing_holder_model
License: All rights reserved
LicenseURL: http://en.wikipedia.org/wiki/All_rights_reserved
objects: App::Link×4, PartDesign::CoordinateSystem×3, PartDesign::SubShapeBinder×2, Part::FeaturePython×2, PartDesign::Body×2, PartDesign::Pad×1, Sketcher::SketchObject×1, PartDesign::Revolution×1, Part::MultiFuse×1, PartDesign::Boolean×1
note: 20 computed .brp shape members not serialized (recipe doc carries the construction recipe); baked Part::Feature solids carry a one-line shape summary decoded from their .brp
EXTERNAL_REF file=composit_stand3_basement_bearing_holder_main.FCStd obj=Sketch
EXTERNAL_REF file=composit_stand3_basement_bearing_holder_main.FCStd obj=Join
EXTERNAL_REF file=composit_stand3_basement_bearing_holder_main.FCStd obj=Placment
EXTERNAL_REF file=../bearing_d100.FCStd obj=Body
EXTERNAL_REF file=composit_stand3_basement_amplifier_main.FCStd obj=Cylinder

FEATURE [PartDesign::SubShapeBinder] Binder
  BindCopyOnChange = 0
  BindMode = 0
  ClaimChildren = false
  Fuse = false
  MakeFace = true
  OffsetFill = false
  OffsetIntersection = false
  OffsetJoinType = 0
  OffsetOpenResult = false
  PartialLoad = false
  Relative = true
  Support = -> [<external composit_stand3_basement_bearing_holder_main.FCStd>#Sketch]
  _Version = 2
FEATURE [PartDesign::SubShapeBinder] Binder001
  BindCopyOnChange = 0
  BindMode = 0
  ClaimChildren = true
  Context = -> Body [Binder001.]
  Fuse = false
  MakeFace = true
  OffsetFill = false
  OffsetIntersection = false
  OffsetJoinType = 0
  OffsetOpenResult = false
  PartialLoad = false
  Relative = false
  Support = -> [Binder]
  _Version = 2
FEATURE [PartDesign::Pad] Pad
  Direction = (0,0,1)
  Length = 18
  Length2 = 10
  Profile = -> Binder001
  Suppressed = false
  Type = 0
FEATURE [App::Link] Link  label="holes_placements"
  LinkedObject = -> <external composit_stand3_basement_bearing_holder_main.FCStd>#Join
FEATURE [App::Link] Link001  label="bearing_placement"
  LinkTransform = true
  LinkedObject = -> <external composit_stand3_basement_bearing_holder_main.FCStd>#Placment
FEATURE [App::Link] Link002  label="Body002"
  LinkedObject = -> <external ../bearing_d100.FCStd>#Body
FEATURE [Part::FeaturePython] Populate001  label="Populate bearing_placement with Body002"  # WARN: FeaturePython — macro-defined, semantics opaque (R4)
  Copying = 0
  ExposePlacement = false
  MarkerShape = 1
  MarkerSize = 0
  NumElements = 0
  Object = -> Link002
  OutputCompounding = 2
  PlacementsTo = -> Link001
  Referencing = 0
  Type = lattice2PopulateCopies.LatticePopulateCopies
  isLattice = 0
FEATURE [App::Link] Link003  label="axis_bolt"
  LinkedObject = -> <external composit_stand3_basement_amplifier_main.FCStd>#Cylinder
FEATURE [PartDesign::CoordinateSystem] Local_CS  label="bottom_LCS"
  AttacherType = Attacher::AttachEngine3D
  AttachmentSupport = -> [XY_Plane]
  MapMode = 5
FEATURE [PartDesign::CoordinateSystem] Local_CS001  label="top_LCS"
  AttacherType = Attacher::AttachEngine3D
  AttachmentOffset = pos=(0,0,18) rot=(0,0,1;0rad)
  AttachmentSupport = -> [XY_Plane]
  MapMode = 5
  Placement = pos=(0,0,18) rot=(0,0,1;0rad)
FEATURE [PartDesign::CoordinateSystem] Local_CS002  label="bearing_LCS"
  AttacherType = Attacher::AttachEngine3D
  AttachmentOffset = pos=(0,0,16) rot=(0,0,1;0rad)
  AttachmentSupport = -> [XY_Plane]
  MapMode = 5
  Placement = pos=(0,0,16) rot=(0,0,1;0rad)
  expr: AttachmentOffset = <<bearing_placement>>.LinkedObject.Placement
FEATURE [Sketcher::SketchObject] Sketch
  ArcFitTolerance = 0
  AttachmentSupport = -> [XZ_Plane001]
  FullyConstrained = true
  MakeInternals = false
  MapMode = 5
  Placement = pos=(0,0,0) rot=(1,0,0;1.5708rad)
  sketch-geometry (9):
    g0: LineSegment StartX=0 StartY=0 StartZ=0 EndX=2.65 EndY=0 EndZ=0
    g1: LineSegment StartX=2.65 StartY=0 StartZ=0 EndX=2.65 EndY=13.6432 EndZ=0
    g2: LineSegment StartX=2.65 StartY=13.6432 StartZ=0 EndX=3.825 EndY=13.6432 EndZ=0
    g3: LineSegment StartX=3.825 StartY=13.6432 StartZ=0 EndX=3.825 EndY=15 EndZ=0
    g4: LineSegment StartX=3.825 StartY=15 StartZ=0 EndX=5 EndY=15 EndZ=0
    g5: LineSegment StartX=5 StartY=15 StartZ=0 EndX=5 EndY=18 EndZ=0
    g6: LineSegment StartX=5 StartY=18 StartZ=0 EndX=0 EndY=18 EndZ=0
    g7: LineSegment StartX=0 StartY=18 StartZ=0 EndX=0 EndY=0 EndZ=0
    g8: LineSegment [constr] StartX=2.65 StartY=13.6432 StartZ=0 EndX=5 EndY=15 EndZ=0
  constraints (25):
    c: Coincident(g-1,g0)
    c: Horizontal(g0)
    c: Coincident(g0,g1)
    c: Vertical(g1)
    c: Coincident(g1,g2)
    c: Horizontal(g2)
    c: Coincident(g2,g3)
    c: Vertical(g3)
    c: Coincident(g3,g4)
    c: Horizontal(g4)
    c: Coincident(g4,g5)
    c: Vertical(g5)
    c: Coincident(g5,g6)
    c: PointOnObject(g6,g-2)
    c: Horizontal(g6)
    c: Coincident(g6,g7)
    c: Coincident(g7,g0)
    c: DistanceY(g7,g7) = 18
    c: Coincident(g8,g1)
    c: Coincident(g8,g4)
    c: Angle(g8) = 0.523599
    c: Equal(g4,g2)
    c: DistanceY(g5,g5) = 3
    c: DistanceX(g0) = 2.65
    c: DistanceX(g6,g6) = 5
FEATURE [PartDesign::Revolution] Revolution
  Angle = 360
  Angle2 = 60
  Axis = (0,2e-16,1)
  Base = (0,0,0)
  Placement = pos=(0,0,0) rot=(1,0,0;1.5708rad)
  Profile = -> Sketch
  ReferenceAxis = -> Sketch [V_Axis]
  Reversed = true
  Suppressed = false
  Type = 0
FEATURE [PartDesign::Body] Body001  label="Body"
  AllowCompound = false
  Group = -> [Sketch,Revolution]
  Origin = -> Origin001
  Tip = -> Revolution
FEATURE [Part::FeaturePython] Populate  label="Populate holes_placements with Cylinder"  # WARN: FeaturePython — macro-defined, semantics opaque (R4)
  Copying = 0
  ExposePlacement = false
  MarkerShape = 1
  MarkerSize = 0
  NumElements = 0
  Object = -> Body001
  OutputCompounding = 1
  PlacementsTo = -> Link
  Referencing = 0
  Type = lattice2PopulateCopies.LatticePopulateCopies
  isLattice = 0
FEATURE [Part::MultiFuse] Fusion
  Shapes = -> [Populate,Populate001,Link003]
FEATURE [PartDesign::Boolean] Boolean
  BaseFeature = -> Pad
  Group = -> [Fusion]
  Suppressed = false
  Type = 1
  UsePlacement = true
FEATURE [PartDesign::Body] Body  label="bearing_holder"
  AllowCompound = false
  Group = -> [Binder001,Pad,Boolean,Local_CS,Local_CS001,Local_CS002]
  Origin = -> Origin
  Tip = -> Boolean
---- part composit_stand3_basement_bottom_PP_model.FCStd = doc fcstd_2923af6e2be5 ----
FCSTD DOCUMENT  (FreeCAD 1.1R38827 (Git))
Label: composit_stand3_basement_bottom_PP_model
License: All rights reserved
LicenseURL: http://en.wikipedia.org/wiki/All_rights_reserved
objects: Part::FeaturePython×11, App::Link×8, Part::Cylinder×4, PartDesign::SubShapeBinder×2, PartDesign::CoordinateSystem×2, Part::Mirroring×1, Part::Compound×1, Part::Offset2D×1, PartDesign::Pad×1, Part::MultiFuse×1, PartDesign::Boolean×1, PartDesign::Body×1
note: 29 computed .brp shape members not serialized (recipe doc carries the construction recipe); baked Part::Feature solids carry a one-line shape summary decoded from their .brp
EXTERNAL_REF file=composit_stand3_basement_bottom_main.FCStd obj=Sketch
EXTERNAL_REF file=composit_stand3_basement_bottom_main.FCStd obj=Placment001
EXTERNAL_REF file=composit_stand3_bar_main.FCStd obj=Placment
EXTERNAL_REF file=composit_stand3_bar_main.FCStd obj=Placment001
EXTERNAL_REF file=composit_stand3_bar_bottom_main.FCStd obj=Join
EXTERNAL_REF file=composit_stand3_basement_bottom_main.FCStd obj=Placment
EXTERNAL_REF file=composit_stand3_basement_bottom_main.FCStd obj=Placment003
EXTERNAL_REF file=composit_stand3_basement_amplifier_main.FCStd obj=Join001
EXTERNAL_REF file=composit_stand3_basement_amplifier_main.FCStd obj=Cylinder

FEATURE [PartDesign::SubShapeBinder] Binder
  BindCopyOnChange = 0
  BindMode = 0
  ClaimChildren = false
  Fuse = false
  MakeFace = true
  OffsetFill = false
  OffsetIntersection = false
  OffsetJoinType = 0
  OffsetOpenResult = false
  PartialLoad = false
  Relative = true
  Support = -> [<external composit_stand3_basement_bottom_main.FCStd>#Sketch]
  _Version = 2
FEATURE [Part::Mirroring] Part__Mirroring  label="Binder (Mirror #1)"
  Base = (0,0,0)
  Normal = (0,1,0)
  Source = -> Binder
FEATURE [Part::Compound] Compound
  Links = -> [Binder,Part__Mirroring]
FEATURE [Part::FeaturePython] PolarArray  # WARN: FeaturePython — macro-defined, semantics opaque (R4)
  Alignment = 0
  AttacherType = Attacher::AttachEngine3D
  CellStart = A1
  Count = 3
  DistributionLaw = 0
  EndInclusive = false
  ExposePlacement = false
  FlipX = false
  FlipZ = false
  GeneratorMode = 0
  MarkerShape = 1
  MarkerSize = 0
  NumElements = 3
  OrientMode = 2
  Radius = 100
  Reverse = false
  SpanEnd = 360
  SpanStart = 0
  Step = 120
  Type = lattice2PolarArray2.PolarArray
  UseArcRadius = false
  UseArcRange = 0
  VSGVersion = 1
  Values = 0.0 | 120.0 | 240.0
  ValuesSource = 2
  isLattice = 1
FEATURE [Part::FeaturePython] Populate  label="Populate PolarArray with Compound"  # WARN: FeaturePython — macro-defined, semantics opaque (R4)
  Copying = 0
  ExposePlacement = false
  MarkerShape = 1
  MarkerSize = 0
  NumElements = 0
  Object = -> Compound
  OutputCompounding = 1
  PlacementsTo = -> PolarArray
  Referencing = 1
  Type = lattice2PopulateCopies.LatticePopulateCopies
  isLattice = 0
FEATURE [Part::FeaturePython] Connect  # WARN: FeaturePython — macro-defined, semantics opaque (R4)
  Objects = -> [Populate]
  Tolerance = 0
FEATURE [Part::Offset2D] Offset2D
  Fill = false
  Intersection = false
  Join = 0
  Mode = 1
  SelfIntersection = false
  Source = -> Connect
  Value = 2
FEATURE [PartDesign::SubShapeBinder] Binder001
  BindCopyOnChange = 0
  BindMode = 0
  ClaimChildren = true
  Context = -> Body [Binder001.]
  Fuse = false
  MakeFace = true
  OffsetFill = false
  OffsetIntersection = false
  OffsetJoinType = 0
  OffsetOpenResult = false
  PartialLoad = false
  Relative = false
  Support = -> [Offset2D]
  _Version = 2
FEATURE [PartDesign::Pad] Pad
  Direction = (0,0,1)
  Length = 3
  Length2 = 10
  Profile = -> Binder001
  Suppressed = false
  Type = 0
FEATURE [PartDesign::CoordinateSystem] Local_CS
  AttacherType = Attacher::AttachEngine3D
  AttachmentSupport = -> [XY_Plane]
  MapMode = 5
FEATURE [PartDesign::CoordinateSystem] Local_CS001
  AttacherType = Attacher::AttachEngine3D
  AttachmentOffset = pos=(0,0,3) rot=(0,0,1;0rad)
  AttachmentSupport = -> [XY_Plane]
  MapMode = 5
  Placement = pos=(0,0,3) rot=(0,0,1;0rad)
FEATURE [App::Link] Link  label="jamb_placement"
  LinkTransform = true
  LinkedObject = -> <external composit_stand3_basement_bottom_main.FCStd>#Placment001
FEATURE [Part::Cylinder] Cylinder
  Angle = 360
  AttacherType = Attacher::AttachEngine3D
  FirstAngle = 0
  Height = 20
  Placement = pos=(0,0,0) rot=(1,0,0;3.14159rad)
  Radius = 4
  SecondAngle = 0
FEATURE [Part::FeaturePython] Populate001  label="Populate jamb_placement with Cylinder"  # WARN: FeaturePython — macro-defined, semantics opaque (R4)
  Copying = 0
  ExposePlacement = false
  MarkerShape = 1
  MarkerSize = 0
  NumElements = 0
  Object = -> Cylinder
  OutputCompounding = 2
  PlacementsTo = -> Link
  Referencing = 0
  Type = lattice2PopulateCopies.LatticePopulateCopies
  isLattice = 0
FEATURE [App::Link] Link001  label="bottom_placement"
  LinkTransform = true
  LinkedObject = -> <external composit_stand3_bar_main.FCStd>#Placment
FEATURE [App::Link] Link002  label="bottom_placement2"
  LinkTransform = true
  LinkedObject = -> <external composit_stand3_bar_main.FCStd>#Placment001
FEATURE [App::Link] Link003  label="bottom_holes_placement"
  LinkedObject = -> <external composit_stand3_bar_bottom_main.FCStd>#Join
FEATURE [Part::FeaturePython] Join  # WARN: FeaturePython — macro-defined, semantics opaque (R4)
  ExposePlacement = false
  Interleave = false
  Links = -> [Link001,Link002]
  MarkerShape = 1
  MarkerSize = 0
  NumElements = 2
  Type = lattice2JoinArrays.JoinArrays
  isLattice = 1
FEATURE [App::Link] Link004  label="bar_placement"
  LinkTransform = true
  LinkedObject = -> <external composit_stand3_basement_bottom_main.FCStd>#Placment
FEATURE [Part::FeaturePython] Populate002  label="Populate PolarArray with bar_placement"  # WARN: FeaturePython — macro-defined, semantics opaque (R4)
  Copying = 0
  ExposePlacement = false
  MarkerShape = 1
  MarkerSize = 0
  NumElements = 3
  Object = -> Link004
  OutputCompounding = 0
  PlacementsTo = -> PolarArray
  Referencing = 1
  Type = lattice2PopulateCopies.LatticePopulateCopies
  isLattice = 1
FEATURE [Part::FeaturePython] Populate003  label="Populate Join with bottom_holes_placement"  # WARN: FeaturePython — macro-defined, semantics opaque (R4)
  Copying = 0
  ExposePlacement = false
  MarkerShape = 1
  MarkerSize = 0
  NumElements = 4
  Object = -> Link003
  OutputCompounding = 0
  PlacementsTo = -> Join
  Referencing = 0
  Type = lattice2PopulateCopies.LatticePopulateCopies
  isLattice = 1
FEATURE [Part::FeaturePython] Populate004  label="Populate Populate PolarArray with bar_placement with Populate Join with bottom_holes_placement"  # WARN: FeaturePython — macro-defined, semantics opaque (R4)
  Copying = 0
  ExposePlacement = false
  MarkerShape = 1
  MarkerSize = 0
  NumElements = 12
  Object = -> Populate003
  OutputCompounding = 0
  PlacementsTo = -> Populate002
  Referencing = 0
  Type = lattice2PopulateCopies.LatticePopulateCopies
  isLattice = 1
FEATURE [Part::Cylinder] Cylinder001
  Angle = 360
  AttacherType = Attacher::AttachEngine3D
  FirstAngle = 0
  Height = 20
  Placement = pos=(0,0,0) rot=(1,0,0;3.14159rad)
  Radius = 2.75
  SecondAngle = 0
FEATURE [Part::FeaturePython] Populate005  label="Populate Populate Populate PolarArray with bar_placement with Populate Join with bottom_holes_placement with Cylinder001"  # WARN: FeaturePython — macro-defined, semantics opaque (R4)
  Copying = 0
  ExposePlacement = false
  MarkerShape = 1
  MarkerSize = 0
  NumElements = 0
  Object = -> Cylinder001
  OutputCompounding = 1
  PlacementsTo = -> Populate004
  Referencing = 0
  Type = lattice2PopulateCopies.LatticePopulateCopies
  isLattice = 0
FEATURE [App::Link] Link005  label="wire_hole_placement"
  LinkTransform = true
  LinkedObject = -> <external composit_stand3_basement_bottom_main.FCStd>#Placment003
FEATURE [Part::Cylinder] Cylinder002  label="hole_8mm"
  Angle = 360
  AttacherType = Attacher::AttachEngine3D
  FirstAngle = 0
  Height = 10
  Radius = 4
  SecondAngle = 0
FEATURE [Part::FeaturePython] Populate006  label="Populate wire_hole_placement with Cylinder002"  # WARN: FeaturePython — macro-defined, semantics opaque (R4)
  Copying = 0
  ExposePlacement = false
  MarkerShape = 1
  MarkerSize = 0
  NumElements = 0
  Object = -> Cylinder002
  OutputCompounding = 2
  PlacementsTo = -> Link005
  Referencing = 0
  Type = lattice2PopulateCopies.LatticePopulateCopies
  isLattice = 0
FEATURE [App::Link] Link006  label="holes_placements"
  LinkedObject = -> <external composit_stand3_basement_amplifier_main.FCStd>#Join001
FEATURE [Part::Cylinder] Cylinder003  label="hole_4mm"
  Angle = 360
  AttacherType = Attacher::AttachEngine3D
  FirstAngle = 0
  Height = 10
  Radius = 2
  SecondAngle = 0
FEATURE [Part::FeaturePython] Populate007  label="Populate holes_placements with hole_4mm"  # WARN: FeaturePython — macro-defined, semantics opaque (R4)
  Copying = 0
  ExposePlacement = false
  MarkerShape = 1
  MarkerSize = 0
  NumElements = 0
  Object = -> Cylinder003
  OutputCompounding = 1
  PlacementsTo = -> Link006
  Referencing = 0
  Type = lattice2PopulateCopies.LatticePopulateCopies
  isLattice = 0
FEATURE [App::Link] Link007  label="axis_bolt"
  LinkedObject = -> <external composit_stand3_basement_amplifier_main.FCStd>#Cylinder
FEATURE [Part::MultiFuse] Fusion
  Shapes = -> [Populate001,Populate005,Populate006,Populate007,Link007]
FEATURE [PartDesign::Boolean] Boolean
  BaseFeature = -> Pad
  Group = -> [Fusion]
  Suppressed = false
  Type = 1
  UsePlacement = true
FEATURE [PartDesign::Body] Body  label="bottom_PP"
  AllowCompound = false
  Group = -> [Binder001,Pad,Local_CS,Local_CS001,Boolean]
  Origin = -> Origin
  Tip = -> Boolean
---- part composit_stand3_basement_bottom_model.FCStd = doc fcstd_d3dcd3c540d6 ----
FCSTD DOCUMENT  (FreeCAD 1.1R38827 (Git))
Label: composit_stand3_basement_bottom_model
License: All rights reserved
LicenseURL: http://en.wikipedia.org/wiki/All_rights_reserved
objects: Part::FeaturePython×16, App::Link×9, PartDesign::CoordinateSystem×4, Part::Cylinder×3, PartDesign::SubShapeBinder×2, PartDesign::Body×2, Part::Mirroring×1, Part::Compound×1, PartDesign::Pad×1, Sketcher::SketchObject×1, PartDesign::Revolution×1, Part::MultiFuse×1, PartDesign::Boolean×1, Part::Feature×1
note: 41 computed .brp shape members not serialized (recipe doc carries the construction recipe); baked Part::Feature solids carry a one-line shape summary decoded from their .brp
EXTERNAL_REF file=composit_stand3_basement_bottom_main.FCStd obj=Sketch
EXTERNAL_REF file=composit_stand3_basement_amplifier_main.FCStd obj=Join001
EXTERNAL_REF file=composit_stand3_basement_amplifier_main.FCStd obj=Cylinder
EXTERNAL_REF file=composit_stand3_basement_bottom_main.FCStd obj=Placment001
EXTERNAL_REF file=composit_stand3_basement_bottom_main.FCStd obj=Placment
EXTERNAL_REF file=composit_stand3_bar_main.FCStd obj=Placment001
EXTERNAL_REF file=composit_stand3_bar_main.FCStd obj=Placment
EXTERNAL_REF file=composit_stand3_bar_bottom_main.FCStd obj=Join
EXTERNAL_REF file=composit_stand3_basement_bottom_main.FCStd obj=Placment002
EXTERNAL_REF file=composit_stand3_basement_bottom_main.FCStd obj=Placment003

FEATURE [PartDesign::SubShapeBinder] Binder
  BindCopyOnChange = 0
  BindMode = 0
  ClaimChildren = true
  Fuse = false
  MakeFace = true
  OffsetFill = false
  OffsetIntersection = false
  OffsetJoinType = 0
  OffsetOpenResult = false
  PartialLoad = false
  Relative = true
  Support = -> [<external composit_stand3_basement_bottom_main.FCStd>#Sketch]
  _Version = 2
FEATURE [Part::Mirroring] Part__Mirroring  label="Binder (Mirror #1)"
  Base = (0,0,0)
  Normal = (0,1,0)
  Source = -> Binder
FEATURE [Part::Compound] Compound
  Links = -> [Binder,Part__Mirroring]
FEATURE [Part::FeaturePython] PolarArray  # WARN: FeaturePython — macro-defined, semantics opaque (R4)
  Alignment = 0
  AttacherType = Attacher::AttachEngine3D
  CellStart = A1
  Count = 3
  DistributionLaw = 0
  EndInclusive = false
  ExposePlacement = false
  FlipX = false
  FlipZ = false
  GeneratorMode = 0
  MarkerShape = 1
  MarkerSize = 0
  NumElements = 3
  OrientMode = 2
  Radius = 25
  Reverse = false
  SpanEnd = 360
  SpanStart = 0
  Step = 120
  Type = lattice2PolarArray2.PolarArray
  UseArcRadius = false
  UseArcRange = 0
  VSGVersion = 1
  Values = 0.0 | 120.0 | 240.0
  ValuesSource = 2
  isLattice = 1
FEATURE [Part::FeaturePython] Populate  label="Populate PolarArray with Compound"  # WARN: FeaturePython — macro-defined, semantics opaque (R4)
  Copying = 0
  ExposePlacement = false
  MarkerShape = 1
  MarkerSize = 0
  NumElements = 0
  Object = -> Compound
  OutputCompounding = 1
  PlacementsTo = -> PolarArray
  Referencing = 1
  Type = lattice2PopulateCopies.LatticePopulateCopies
  isLattice = 0
FEATURE [Part::FeaturePython] Connect  # WARN: FeaturePython — macro-defined, semantics opaque (R4)
  Objects = -> [Populate]
  Tolerance = 0
FEATURE [PartDesign::SubShapeBinder] Binder001
  BindCopyOnChange = 0
  BindMode = 0
  ClaimChildren = true
  Context = -> Body [Binder001.]
  Fuse = false
  MakeFace = false
  OffsetFill = false
  OffsetIntersection = false
  OffsetJoinType = 0
  OffsetOpenResult = false
  PartialLoad = false
  Relative = false
  Support = -> [Connect]
  _Version = 2
FEATURE [PartDesign::Pad] Pad
  Direction = (0,0,1)
  Length = 18
  Length2 = 10
  Profile = -> Binder001
  Refine = true
  Suppressed = false
  Type = 0
FEATURE [App::Link] Link  label="holes_placements"
  LinkedObject = -> <external composit_stand3_basement_amplifier_main.FCStd>#Join001
FEATURE [Part::Cylinder] Cylinder  label="hole_3.2mm"
  Angle = 360
  AttacherType = Attacher::AttachEngine3D
  FirstAngle = 0
  Height = 18
  Radius = 1.6
  SecondAngle = 0
FEATURE [Part::FeaturePython] Populate001  label="Populate holes_placements with Cylinder"  # WARN: FeaturePython — macro-defined, semantics opaque (R4)
  Copying = 0
  ExposePlacement = false
  MarkerShape = 1
  MarkerSize = 0
  NumElements = 0
  Object = -> Cylinder
  OutputCompounding = 1
  PlacementsTo = -> Link
  Referencing = 0
  Type = lattice2PopulateCopies.LatticePopulateCopies
  isLattice = 0
FEATURE [App::Link] Link001  label="axis_bolt"
  LinkedObject = -> <external composit_stand3_basement_amplifier_main.FCStd>#Cylinder
FEATURE [Sketcher::SketchObject] Sketch
  ArcFitTolerance = 0
  AttachmentSupport = -> [XZ_Plane002]
  FullyConstrained = true
  MakeInternals = false
  MapMode = 5
  Placement = pos=(0,0,0) rot=(1,0,0;1.5708rad)
  expr: Constraints[9] = 28.5 / 2
  sketch-geometry (4):
    g0: LineSegment StartX=0 StartY=0 StartZ=0 EndX=14.25 EndY=0 EndZ=0
    g1: LineSegment StartX=14.25 StartY=0 StartZ=0 EndX=14.25 EndY=10 EndZ=0
    g2: LineSegment StartX=14.25 StartY=10 StartZ=0 EndX=0 EndY=10 EndZ=0
    g3: LineSegment StartX=0 StartY=10 StartZ=0 EndX=0 EndY=0 EndZ=0
  constraints (11):
    c: Coincident(g0,g1)
    c: Coincident(g1,g2)
    c: Coincident(g2,g3)
    c: Coincident(g3,g0)
    c: Horizontal(g0)
    c: Horizontal(g2)
    c: Vertical(g1)
    c: Vertical(g3)
    c: Coincident(g0,g-1)
    c: DistanceX(g1) = 14.25
    c: DistanceY(g1) = 10
FEATURE [PartDesign::Revolution] Revolution
  Angle = 360
  Angle2 = 60
  Axis = (0,2e-16,1)
  Base = (0,0,0)
  Placement = pos=(0,0,0) rot=(1,0,0;1.5708rad)
  Profile = -> Sketch
  ReferenceAxis = -> Sketch [V_Axis]
  Reversed = true
  Suppressed = false
  Type = 0
FEATURE [PartDesign::Body] Body002  label="bearing_small"
  AllowCompound = false
  Group = -> [Sketch,Revolution]
  Origin = -> Origin002
  Placement = pos=(0,0,-8) rot=(0,0,1;0rad)
  Tip = -> Revolution
FEATURE [PartDesign::CoordinateSystem] Local_CS  label="bottom_LCS"
  AttacherType = Attacher::AttachEngine3D
  AttachmentSupport = -> [XY_Plane]
  MapMode = 5
FEATURE [PartDesign::CoordinateSystem] Local_CS001  label="top_LCS"
  AttacherType = Attacher::AttachEngine3D
  AttachmentOffset = pos=(0,0,18) rot=(0,0,1;0rad)
  AttachmentSupport = -> [XY_Plane]
  MapMode = 5
  Placement = pos=(0,0,18) rot=(0,0,1;0rad)
FEATURE [App::Link] Link002  label="jamb_placement"
  LinkTransform = true
  LinkedObject = -> <external composit_stand3_basement_bottom_main.FCStd>#Placment001
FEATURE [Part::Cylinder] Cylinder001  label="hole_8mm"
  Angle = 360
  AttacherType = Attacher::AttachEngine3D
  FirstAngle = 0
  Height = 18
  Placement = pos=(0,0,0) rot=(1,0,0;3.14159rad)
  Radius = 4
  SecondAngle = 0
FEATURE [Part::FeaturePython] Populate002  label="Populate jamb_placement with hole_8mm"  # WARN: FeaturePython — macro-defined, semantics opaque (R4)
  Copying = 0
  ExposePlacement = false
  MarkerShape = 1
  MarkerSize = 0
  NumElements = 0
  Object = -> Cylinder001
  OutputCompounding = 2
  PlacementsTo = -> Link002
  Referencing = 0
  Type = lattice2PopulateCopies.LatticePopulateCopies
  isLattice = 0
FEATURE [PartDesign::CoordinateSystem] Local_CS002
  AttacherType = Attacher::AttachEngine3D
  AttachmentOffset = pos=(215,0,21) rot=(0,0,1;0rad)
  AttachmentSupport = -> [XY_Plane]
  MapMode = 5
  Placement = pos=(215,0,21) rot=(0,0,1;0rad)
  expr: AttachmentOffset = <<jamb_placement>>.LinkedObject.Placement * placement(vector(0; 0; 3); rotation(0; 0; 0))
FEATURE [App::Link] Link003  label="bar_placement"
  LinkTransform = true
  LinkedObject = -> <external composit_stand3_basement_bottom_main.FCStd>#Placment
FEATURE [Part::FeaturePython] Populate003  label="Populate PolarArray with bar_placement"  # WARN: FeaturePython — macro-defined, semantics opaque (R4)
  Copying = 0
  ExposePlacement = false
  MarkerShape = 1
  MarkerSize = 0
  NumElements = 3
  Object = -> Link003
  OutputCompounding = 0
  PlacementsTo = -> PolarArray
  Referencing = 1
  Type = lattice2PopulateCopies.LatticePopulateCopies
  isLattice = 1
FEATURE [App::Link] Link004  label="bottom_placement2"
  LinkTransform = true
  LinkedObject = -> <external composit_stand3_bar_main.FCStd>#Placment001
FEATURE [App::Link] Link005  label="bottom_placement"
  LinkTransform = true
  LinkedObject = -> <external composit_stand3_bar_main.FCStd>#Placment
FEATURE [Part::FeaturePython] Join  # WARN: FeaturePython — macro-defined, semantics opaque (R4)
  ExposePlacement = false
  Interleave = false
  Links = -> [Link005,Link004]
  MarkerShape = 1
  MarkerSize = 0
  NumElements = 2
  Type = lattice2JoinArrays.JoinArrays
  isLattice = 1
FEATURE [App::Link] Link006  label="bottom_holes_placement"
  LinkedObject = -> <external composit_stand3_bar_bottom_main.FCStd>#Join
FEATURE [Part::FeaturePython] Populate004  label="Populate Join with bottom_holes_placement"  # WARN: FeaturePython — macro-defined, semantics opaque (R4)
  Copying = 0
  ExposePlacement = false
  MarkerShape = 1
  MarkerSize = 0
  NumElements = 4
  Object = -> Link006
  OutputCompounding = 0
  PlacementsTo = -> Join
  Referencing = 0
  Type = lattice2PopulateCopies.LatticePopulateCopies
  isLattice = 1
FEATURE [Part::FeaturePython] Populate005  label="Populate Populate PolarArray with bar_placement with Populate Join with bottom_holes_placement"  # WARN: FeaturePython — macro-defined, semantics opaque (R4)
  Copying = 0
  ExposePlacement = false
  MarkerShape = 1
  MarkerSize = 0
  NumElements = 12
  Object = -> Populate004
  OutputCompounding = 0
  PlacementsTo = -> Populate003
  Referencing = 0
  Type = lattice2PopulateCopies.LatticePopulateCopies
  isLattice = 1
FEATURE [Part::Cylinder] Cylinder002  label="hole_5.5mm"
  Angle = 360
  AttacherType = Attacher::AttachEngine3D
  FirstAngle = 0
  Height = 20
  Placement = pos=(0,0,0) rot=(1,0,0;3.14159rad)
  Radius = 2.75
  SecondAngle = 0
FEATURE [Part::FeaturePython] Populate006  label="Populate Populate Populate PolarArray with bar_placement with Populate Join with bottom_holes_placement with hole_5.5mm"  # WARN: FeaturePython — macro-defined, semantics opaque (R4)
  Copying = 0
  ExposePlacement = false
  MarkerShape = 1
  MarkerSize = 0
  NumElements = 0
  Object = -> Cylinder002
  OutputCompounding = 1
  PlacementsTo = -> Populate005
  Referencing = 0
  Type = lattice2PopulateCopies.LatticePopulateCopies
  isLattice = 0
FEATURE [PartDesign::CoordinateSystem] Local_CS003  label="bar_LCS"
  AttacherType = Attacher::AttachEngine3D
  AttachmentOffset = pos=(383.5,0,21) rot=(0,0,1;3.14159rad)
  AttachmentSupport = -> [XY_Plane]
  MapMode = 5
  Placement = pos=(383.5,0,21) rot=(0,0,1;3.14159rad)
  expr: AttachmentOffset = <<bar_placement>>.LinkedObject.Placement * placement(vector(0; 0; 3); rotation(0; 0; 0))
FEATURE [App::Link] Link007  label="wheel_placement"
  LinkTransform = true
  LinkedObject = -> <external composit_stand3_basement_bottom_main.FCStd>#Placment002
FEATURE [Part::FeaturePython] PolarArray001  # WARN: FeaturePython — macro-defined, semantics opaque (R4)
  Alignment = 0
  AttacherType = Attacher::AttachEngine3D
  CellStart = A1
  Count = 4
  DistributionLaw = 0
  EndInclusive = false
  ExposePlacement = false
  FlipX = false
  FlipZ = false
  GeneratorMode = 0
  MarkerShape = 1
  MarkerSize = 0
  NumElements = 4
  OrientMode = 2
  Placement = pos=(0,0,0) rot=(0,0,1;0.785398rad)
  Radius = 28.2843
  Reverse = false
  SpanEnd = 360
  SpanStart = 0
  Step = 90
  Type = lattice2PolarArray2.PolarArray
  UseArcRadius = false
  UseArcRange = 0
  VSGVersion = 1
  Values = 0.0 | 90.0 | 180.0 | 270.0
  ValuesSource = 2
  isLattice = 1
  expr: Radius = 20 mm * sqrt(2)
FEATURE [Part::FeaturePython] Populate007  label="Populate PolarArray with wheel_placement"  # WARN: FeaturePython — macro-defined, semantics opaque (R4)
  Copying = 0
  ExposePlacement = false
  MarkerShape = 1
  MarkerSize = 0
  NumElements = 3
  Object = -> Link007
  OutputCompounding = 0
  PlacementsTo = -> PolarArray
  Referencing = 1
  Type = lattice2PopulateCopies.LatticePopulateCopies
  isLattice = 1
FEATURE [Part::FeaturePython] Populate008  label="Populate Populate PolarArray with wheel_placement with PolarArray001"  # WARN: FeaturePython — macro-defined, semantics opaque (R4)
  Copying = 0
  ExposePlacement = false
  MarkerShape = 1
  MarkerSize = 0
  NumElements = 12
  Object = -> PolarArray001
  OutputCompounding = 0
  PlacementsTo = -> Populate007
  Referencing = 0
  Type = lattice2PopulateCopies.LatticePopulateCopies
  isLattice = 1
FEATURE [Part::FeaturePython] Populate009  label="Populate Populate Populate PolarArray with wheel_placement with PolarArray001 with hole_3.2mm"  # WARN: FeaturePython — macro-defined, semantics opaque (R4)
  Copying = 0
  ExposePlacement = false
  MarkerShape = 1
  MarkerSize = 0
  NumElements = 0
  Object = -> Cylinder
  OutputCompounding = 1
  PlacementsTo = -> Populate008
  Referencing = 0
  Type = lattice2PopulateCopies.LatticePopulateCopies
  isLattice = 0
FEATURE [App::Link] Link008  label="wire_hole_placement"
  LinkPlacement = pos=(0,0,18) rot=(0,0,1;0rad)
  LinkTransform = true
  LinkedObject = -> <external composit_stand3_basement_bottom_main.FCStd>#Placment003
  Placement = pos=(0,0,18) rot=(0,0,1;0rad)
FEATURE [Part::FeaturePython] Populate010  label="Populate PolarArray with wire_hole_placement"  # WARN: FeaturePython — macro-defined, semantics opaque (R4)
  Copying = 0
  ExposePlacement = false
  MarkerShape = 1
  MarkerSize = 0
  NumElements = 3
  Object = -> Link008
  OutputCompounding = 0
  PlacementsTo = -> PolarArray
  Referencing = 1
  Type = lattice2PopulateCopies.LatticePopulateCopies
  isLattice = 1
FEATURE [Part::FeaturePython] Populate011  label="Populate Populate PolarArray with wire_hole_placement with hole_8mm"  # WARN: FeaturePython — macro-defined, semantics opaque (R4)
  Copying = 0
  ExposePlacement = false
  MarkerShape = 1
  MarkerSize = 0
  NumElements = 0
  Object = -> Cylinder001
  OutputCompounding = 1
  PlacementsTo = -> Link008
  Referencing = 0
  Type = lattice2PopulateCopies.LatticePopulateCopies
  isLattice = 0
FEATURE [Part::MultiFuse] Fusion
  Shapes = -> [Populate001,Link001,Body002,Populate002,Populate006,Populate009,Populate011]
FEATURE [PartDesign::Boolean] Boolean
  BaseFeature = -> Pad
  Group = -> [Fusion]
  Suppressed = false
  Type = 1
  UsePlacement = true
FEATURE [PartDesign::Body] Body  label="bottom"
  AllowCompound = false
  Group = -> [Binder001,Pad,Boolean,Local_CS,Local_CS001,Local_CS002,Local_CS003]
  Origin = -> Origin
  Tip = -> Boolean
FEATURE [Part::Feature] Body003  label="bottom001"
  shape: bbox 604.9 x 690.2 x 18 mm, 57 faces (baked)
---- part composit_stand3_basement_top_PP_model.FCStd = doc fcstd_8e599816840b ----
FCSTD DOCUMENT  (FreeCAD 1.1R38827 (Git))
Label: composit_stand3_basement_top_PP_model
License: All rights reserved
LicenseURL: http://en.wikipedia.org/wiki/All_rights_reserved
objects: Part::FeaturePython×7, App::Link×3, PartDesign::SubShapeBinder×2, PartDesign::CoordinateSystem×2, Part::Mirroring×1, Part::Compound×1, Part::Offset2D×1, PartDesign::Pad×1, Part::Cylinder×1, Part::Extrusion×1, Part::MultiFuse×1, PartDesign::Boolean×1, PartDesign::Body×1
note: 23 computed .brp shape members not serialized (recipe doc carries the construction recipe); baked Part::Feature solids carry a one-line shape summary decoded from their .brp
EXTERNAL_REF file=composit_stand3_basement_top_main.FCStd obj=Sketch
EXTERNAL_REF file=composit_stand3_basin_holder_main.FCStd obj=Join
EXTERNAL_REF file=../U-fix.FCStd obj=Sketch002
EXTERNAL_REF file=composit_stand3_base_part1_main.FCStd obj=Placment003

FEATURE [PartDesign::SubShapeBinder] Binder
  BindCopyOnChange = 0
  BindMode = 0
  ClaimChildren = true
  Fuse = false
  MakeFace = true
  OffsetFill = false
  OffsetIntersection = false
  OffsetJoinType = 0
  OffsetOpenResult = false
  PartialLoad = false
  Relative = true
  Support = -> [<external composit_stand3_basement_top_main.FCStd>#Sketch]
  _Version = 2
FEATURE [Part::FeaturePython] PolarArray  # WARN: FeaturePython — macro-defined, semantics opaque (R4)
  Alignment = 0
  AttacherType = Attacher::AttachEngine3D
  CellStart = A1
  Count = 3
  DistributionLaw = 0
  EndInclusive = false
  ExposePlacement = false
  FlipX = false
  FlipZ = false
  GeneratorMode = 0
  MarkerShape = 1
  MarkerSize = 0
  NumElements = 3
  OrientMode = 2
  Radius = 100
  Reverse = false
  SpanEnd = 360
  SpanStart = 0
  Step = 120
  Type = lattice2PolarArray2.PolarArray
  UseArcRadius = false
  UseArcRange = 0
  VSGVersion = 1
  Values = 0.0 | 120.0 | 240.0
  ValuesSource = 2
  isLattice = 1
FEATURE [Part::Mirroring] Part__Mirroring  label="Binder (Mirror #1)"
  Base = (0,0,0)
  Normal = (0,1,0)
  Source = -> Binder
FEATURE [Part::Compound] Compound
  Links = -> [Binder,Part__Mirroring]
FEATURE [Part::FeaturePython] Populate  label="Populate PolarArray with Compound"  # WARN: FeaturePython — macro-defined, semantics opaque (R4)
  Copying = 0
  ExposePlacement = false
  MarkerShape = 1
  MarkerSize = 0
  NumElements = 0
  Object = -> Compound
  OutputCompounding = 1
  PlacementsTo = -> PolarArray
  Referencing = 1
  Type = lattice2PopulateCopies.LatticePopulateCopies
  isLattice = 0
FEATURE [Part::FeaturePython] Connect  # WARN: FeaturePython — macro-defined, semantics opaque (R4)
  Objects = -> [Populate]
  Tolerance = 0
FEATURE [Part::Offset2D] Offset2D
  Fill = false
  Intersection = false
  Join = 0
  Mode = 1
  SelfIntersection = false
  Source = -> Connect
  Value = 2
FEATURE [PartDesign::SubShapeBinder] Binder001
  BindCopyOnChange = 0
  BindMode = 0
  ClaimChildren = true
  Context = -> Body [Binder001.]
  Fuse = false
  MakeFace = true
  OffsetFill = false
  OffsetIntersection = false
  OffsetJoinType = 0
  OffsetOpenResult = false
  PartialLoad = false
  Relative = true
  Support = -> [Offset2D]
  _Version = 2
FEATURE [PartDesign::Pad] Pad
  Direction = (0,0,1)
  Length = 3
  Length2 = 10
  Profile = -> Binder001
  Refine = true
  Suppressed = false
  Type = 0
FEATURE [Part::Cylinder] Cylinder  label="hole_3.4mm"
  Angle = 360
  AttacherType = Attacher::AttachEngine3D
  FirstAngle = 0
  Height = 10
  Radius = 1.7
  SecondAngle = 0
FEATURE [App::Link] Link  label="holes"
  LinkedObject = -> <external composit_stand3_basin_holder_main.FCStd>#Join
FEATURE [Part::FeaturePython] Populate001  label="Populate holes with hole_3.4mm"  # WARN: FeaturePython — macro-defined, semantics opaque (R4)
  Copying = 0
  ExposePlacement = false
  MarkerShape = 1
  MarkerSize = 0
  NumElements = 0
  Object = -> Cylinder
  OutputCompounding = 1
  PlacementsTo = -> Link
  Referencing = 0
  Type = lattice2PopulateCopies.LatticePopulateCopies
  isLattice = 0
FEATURE [PartDesign::CoordinateSystem] Local_CS  label="bottom_LCS"
  AttacherType = Attacher::AttachEngine3D
  AttachmentSupport = -> [XY_Plane]
  MapMode = 5
FEATURE [PartDesign::CoordinateSystem] Local_CS001  label="top_LCS"
  AttacherType = Attacher::AttachEngine3D
  AttachmentOffset = pos=(0,0,3) rot=(0,0,1;0rad)
  AttachmentSupport = -> [XY_Plane]
  MapMode = 5
  Placement = pos=(0,0,3) rot=(0,0,1;0rad)
FEATURE [App::Link] Link001  label="holes_bottom"
  LinkedObject = -> <external ../U-fix.FCStd>#Sketch002
FEATURE [Part::Extrusion] Extrude
  Base = -> Link001
  Dir = (0,0,1)
  DirMode = 2
  FaceMakerClass = Part::FaceMakerBullseye
  FaceMakerMode = 3
  LengthFwd = 10
  LengthRev = 0
  Solid = true
  Symmetric = false
FEATURE [App::Link] Link002  label="bottom_fix_placement"
  LinkTransform = true
  LinkedObject = -> <external composit_stand3_base_part1_main.FCStd>#Placment003
FEATURE [Part::FeaturePython] PolarArray001  # WARN: FeaturePython — macro-defined, semantics opaque (R4)
  Alignment = 0
  AttacherType = Attacher::AttachEngine3D
  CellStart = A1
  Count = 3
  DistributionLaw = 0
  EndInclusive = false
  ExposePlacement = false
  FlipX = false
  FlipZ = false
  GeneratorMode = 0
  MarkerShape = 1
  MarkerSize = 0
  NumElements = 3
  OrientMode = 2
  Radius = 250
  Reverse = false
  SpanEnd = 360
  SpanStart = 0
  Step = 120
  Type = lattice2PolarArray2.PolarArray
  UseArcRadius = false
  UseArcRange = 0
  VSGVersion = 1
  Values = 0.0 | 120.0 | 240.0
  ValuesSource = 2
  isLattice = 1
FEATURE [Part::FeaturePython] Populate002  label="Populate PolarArray001 with bottom_fix_placement"  # WARN: FeaturePython — macro-defined, semantics opaque (R4)
  Copying = 0
  ExposePlacement = false
  MarkerShape = 1
  MarkerSize = 0
  NumElements = 3
  Object = -> Link002
  OutputCompounding = 0
  PlacementsTo = -> PolarArray001
  Referencing = 1
  Type = lattice2PopulateCopies.LatticePopulateCopies
  isLattice = 1
FEATURE [Part::FeaturePython] Populate003  label="Populate Populate PolarArray001 with bottom_fix_placement with Extrude"  # WARN: FeaturePython — macro-defined, semantics opaque (R4)
  Copying = 0
  ExposePlacement = false
  MarkerShape = 1
  MarkerSize = 0
  NumElements = 0
  Object = -> Extrude
  OutputCompounding = 1
  PlacementsTo = -> Populate002
  Referencing = 0
  Type = lattice2PopulateCopies.LatticePopulateCopies
  isLattice = 0
FEATURE [Part::MultiFuse] Fusion
  Shapes = -> [Populate001,Populate003]
FEATURE [PartDesign::Boolean] Boolean
  BaseFeature = -> Pad
  Group = -> [Fusion]
  Suppressed = false
  Type = 1
  UsePlacement = true
FEATURE [PartDesign::Body] Body  label="top_PP"
  AllowCompound = false
  Group = -> [Binder001,Pad,Boolean,Local_CS,Local_CS001]
  Origin = -> Origin
  Tip = -> Boolean
---- part composit_stand3_basement_top_model.FCStd = doc fcstd_1554d6b0dc08 ----
FCSTD DOCUMENT  (FreeCAD 1.1R38827 (Git))
Label: composit_stand3_basement_top_model
License: All rights reserved
LicenseURL: http://en.wikipedia.org/wiki/All_rights_reserved
objects: Part::FeaturePython×11, App::Link×6, PartDesign::SubShapeBinder×4, PartDesign::Body×3, PartDesign::CoordinateSystem×3, PartDesign::Pad×2, Part::Offset2D×2, Part::Face×2, Part::Cylinder×2, Part::Mirroring×1, Part::Compound×1, Sketcher::SketchObject×1, PartDesign::AdditivePipe×1, Part::Cut×1, Part::Extrusion×1, Part::MultiFuse×1, PartDesign::Boolean×1
note: 45 computed .brp shape members not serialized (recipe doc carries the construction recipe); baked Part::Feature solids carry a one-line shape summary decoded from their .brp
EXTERNAL_REF file=composit_stand3_basement_top_main.FCStd obj=Sketch
EXTERNAL_REF file=composit_stand3_basement_amplifier_main.FCStd obj=Join001
EXTERNAL_REF file=composit_stand3_basement_bottom_main.FCStd obj=Placment001
EXTERNAL_REF file=../jamb_corner.FCStd obj=Join
EXTERNAL_REF file=../U-fix.FCStd obj=Sketch002
EXTERNAL_REF file=composit_stand3_base_part1_main.FCStd obj=Placment003
EXTERNAL_REF file=composit_stand3_basin_holder_main.FCStd obj=Join

FEATURE [PartDesign::SubShapeBinder] Binder
  BindCopyOnChange = 0
  BindMode = 0
  ClaimChildren = true
  Fuse = false
  MakeFace = true
  OffsetFill = false
  OffsetIntersection = false
  OffsetJoinType = 0
  OffsetOpenResult = false
  PartialLoad = false
  Relative = true
  Support = -> [<external composit_stand3_basement_top_main.FCStd>#Sketch]
  _Version = 2
FEATURE [Part::FeaturePython] PolarArray  # WARN: FeaturePython — macro-defined, semantics opaque (R4)
  Alignment = 0
  AttacherType = Attacher::AttachEngine3D
  CellStart = A1
  Count = 3
  DistributionLaw = 0
  EndInclusive = false
  ExposePlacement = false
  FlipX = false
  FlipZ = false
  GeneratorMode = 0
  MarkerShape = 1
  MarkerSize = 0
  NumElements = 3
  OrientMode = 2
  Radius = 50
  Reverse = false
  SpanEnd = 360
  SpanStart = 0
  Step = 120
  Type = lattice2PolarArray2.PolarArray
  UseArcRadius = false
  UseArcRange = 0
  VSGVersion = 1
  Values = 0.0 | 120.0 | 240.0
  ValuesSource = 2
  isLattice = 1
FEATURE [Part::Mirroring] Part__Mirroring  label="Binder (Mirror #1)"
  Base = (0,0,0)
  Normal = (0,1,0)
  Source = -> Binder
FEATURE [Part::Compound] Compound
  Links = -> [Binder,Part__Mirroring]
FEATURE [Part::FeaturePython] Populate  label="Populate PolarArray with Compound"  # WARN: FeaturePython — macro-defined, semantics opaque (R4)
  Copying = 0
  ExposePlacement = false
  MarkerShape = 1
  MarkerSize = 0
  NumElements = 0
  Object = -> Compound
  OutputCompounding = 1
  PlacementsTo = -> PolarArray
  Referencing = 1
  Type = lattice2PopulateCopies.LatticePopulateCopies
  isLattice = 0
FEATURE [Part::FeaturePython] Connect  # WARN: FeaturePython — macro-defined, semantics opaque (R4)
  Objects = -> [Populate]
  Tolerance = 0
FEATURE [PartDesign::SubShapeBinder] Binder001
  BindCopyOnChange = 0
  BindMode = 0
  ClaimChildren = true
  Context = -> Body [Binder001.]
  Fuse = false
  MakeFace = true
  OffsetFill = false
  OffsetIntersection = false
  OffsetJoinType = 0
  OffsetOpenResult = false
  PartialLoad = false
  Relative = true
  Support = -> [Connect]
  _Version = 2
FEATURE [PartDesign::Pad] Pad
  Direction = (0,0,1)
  Length = 18
  Length2 = 10
  Profile = -> Binder001
  Suppressed = false
  Type = 0
FEATURE [Sketcher::SketchObject] Sketch
  ArcFitTolerance = 0
  AttachmentOffset = pos=(349.171,0,0) rot=(0,0,1;0rad)
  AttachmentSupport = -> [XZ_Plane001]
  FullyConstrained = true
  MakeInternals = false
  MapMode = 5
  Placement = pos=(349.171,0,0) rot=(1,0,0;1.5708rad)
  expr: .AttachmentOffset.Base.x = <<composit_stand3_basement_top_main>>#<<basement_top_main_sketch>>.Constraints.max_r
  sketch-geometry (3):
    g0: LineSegment StartX=0 StartY=0 StartZ=0 EndX=0 EndY=15 EndZ=0
    g1: LineSegment StartX=0 StartY=15 StartZ=0 EndX=-15 EndY=0 EndZ=0
    g2: LineSegment StartX=-15 StartY=0 StartZ=0 EndX=0 EndY=0 EndZ=0
  constraints (8):
    c: Coincident(g-1,g0)
    c: PointOnObject(g0,g-2)
    c: Coincident(g0,g1)
    c: PointOnObject(g1,g-1)
    c: Coincident(g1,g2)
    c: Coincident(g2,g0)
    c: Equal(g2,g0)
    c: DistanceY(g0,g0) = 15
FEATURE [PartDesign::SubShapeBinder] Binder002
  BindCopyOnChange = 0
  BindMode = 0
  ClaimChildren = true
  Context = -> Body001 [Binder002.]
  Fuse = false
  MakeFace = false
  OffsetFill = false
  OffsetIntersection = false
  OffsetJoinType = 0
  OffsetOpenResult = false
  PartialLoad = false
  Relative = false
  Support = -> [Connect]
  _Version = 2
FEATURE [PartDesign::AdditivePipe] AdditivePipe
  AuxilleryCurvelinear = true
  AuxillerySpineTangent = false
  Binormal = (0,0,0)
  Mode = 0
  Placement = pos=(0,0,0) rot=(1,0,0;1.5708rad)
  Profile = -> Sketch
  Refine = true
  Spine = -> Binder002
  SpineTangent = false
  Suppressed = false
  Transformation = 0
  Transition = 0
FEATURE [PartDesign::Body] Body001
  AllowCompound = false
  Group = -> [Sketch,Binder002,AdditivePipe]
  Origin = -> Origin001
  Tip = -> AdditivePipe
FEATURE [Part::Offset2D] Offset2D
  Fill = false
  Intersection = false
  Join = 0
  Mode = 1
  SelfIntersection = false
  Source = -> Connect
  Value = -25
FEATURE [Part::Offset2D] Offset2D001
  Fill = false
  Intersection = false
  Join = 0
  Mode = 1
  SelfIntersection = false
  Source = -> Offset2D
  Value = -5
FEATURE [Part::Face] Face
  FaceMakerClass = Part::FaceMakerBullseye
  Sources = -> [Offset2D]
FEATURE [Part::Face] Face001
  FaceMakerClass = Part::FaceMakerBullseye
  Sources = -> [Offset2D001]
FEATURE [Part::Cut] Cut
  Base = -> Face
  Tool = -> Face001
FEATURE [PartDesign::SubShapeBinder] Binder003
  BindCopyOnChange = 0
  BindMode = 0
  ClaimChildren = true
  Context = -> Body002 [Binder003.]
  Fuse = false
  MakeFace = true
  OffsetFill = false
  OffsetIntersection = false
  OffsetJoinType = 0
  OffsetOpenResult = false
  PartialLoad = false
  Relative = true
  Support = -> [Cut]
  _Version = 2
FEATURE [PartDesign::Pad] Pad001
  Direction = (0,0,1)
  Length = 5
  Length2 = 10
  Profile = -> Binder003
  Suppressed = false
  Type = 0
FEATURE [PartDesign::Body] Body002
  AllowCompound = false
  Group = -> [Binder003,Pad001]
  Origin = -> Origin002
  Tip = -> Pad001
FEATURE [App::Link] Link  label="amplifier_holes_placements"
  LinkedObject = -> <external composit_stand3_basement_amplifier_main.FCStd>#Join001
FEATURE [Part::Cylinder] Cylinder  label="hole_3.2mm"
  Angle = 360
  AttacherType = Attacher::AttachEngine3D
  FirstAngle = 0
  Height = 18
  Radius = 1.6
  SecondAngle = 0
FEATURE [PartDesign::CoordinateSystem] Local_CS  label="bottom_LCS"
  AttacherType = Attacher::AttachEngine3D
  AttachmentSupport = -> [XY_Plane]
  MapMode = 5
FEATURE [PartDesign::CoordinateSystem] Local_CS001  label="top_LCS"
  AttacherType = Attacher::AttachEngine3D
  AttachmentOffset = pos=(0,0,18) rot=(0,0,1;0rad)
  AttachmentSupport = -> [XY_Plane]
  MapMode = 5
  Placement = pos=(0,0,18) rot=(0,0,1;0rad)
FEATURE [App::Link] Link001  label="jamb_placement"
  LinkTransform = true
  LinkedObject = -> <external composit_stand3_basement_bottom_main.FCStd>#Placment001
FEATURE [Part::FeaturePython] Placment  label="corner_placement"  # WARN: FeaturePython — macro-defined, semantics opaque (R4)
  AttacherType = Attacher::AttachEngine3D
  ExposePlacement = true
  MarkerShape = 1
  MarkerSize = 50
  NumElements = 1
  Placement = pos=(0,-2.1,-18) rot=(0,0,1;1.5708rad)
  Type = lattice2AttachablePlacement.AttachablePlacement
  isLattice = 1
FEATURE [App::Link] Link002  label="holes_hor"
  LinkedObject = -> <external ../jamb_corner.FCStd>#Join
FEATURE [Part::FeaturePython] Populate002  label="Populate jamb_placement with corner_placement"  # WARN: FeaturePython — macro-defined, semantics opaque (R4)
  Copying = 0
  ExposePlacement = false
  MarkerShape = 1
  MarkerSize = 50
  NumElements = 1
  Object = -> Placment
  OutputCompounding = 0
  PlacementsTo = -> Link001
  Referencing = 0
  Type = lattice2PopulateCopies.LatticePopulateCopies
  isLattice = 1
FEATURE [Part::FeaturePython] Populate003  label="Populate Populate jamb_placement with corner_placement with holes_hor"  # WARN: FeaturePython — macro-defined, semantics opaque (R4)
  Copying = 0
  ExposePlacement = false
  MarkerShape = 1
  MarkerSize = 0
  NumElements = 3
  Object = -> Link002
  OutputCompounding = 0
  PlacementsTo = -> Populate002
  Referencing = 0
  Type = lattice2PopulateCopies.LatticePopulateCopies
  isLattice = 1
FEATURE [Part::FeaturePython] Join  # WARN: FeaturePython — macro-defined, semantics opaque (R4)
  ExposePlacement = false
  Interleave = false
  Links = -> [Populate003,Link]
  MarkerShape = 1
  MarkerSize = 0
  NumElements = 17
  Type = lattice2JoinArrays.JoinArrays
  isLattice = 1
FEATURE [Part::FeaturePython] Populate001  label="Populate holes_placements with Cylinder"  # WARN: FeaturePython — macro-defined, semantics opaque (R4)
  Copying = 0
  ExposePlacement = false
  MarkerShape = 1
  MarkerSize = 0
  NumElements = 0
  Object = -> Cylinder
  OutputCompounding = 1
  PlacementsTo = -> Join
  Referencing = 0
  Type = lattice2PopulateCopies.LatticePopulateCopies
  isLattice = 0
FEATURE [PartDesign::CoordinateSystem] Local_CS002  label="jamb_LCS"
  AttacherType = Attacher::AttachEngine3D
  AttachmentOffset = pos=(0,0,0) rot=(0.707107,-0.707107,0;3.14159rad)
  AttachmentSupport = -> [Populate002]
  MapMode = 7
  Placement = pos=(215,-2.1,0) rot=(0.57735,-0.57735,-0.57735;4.18879rad)
FEATURE [App::Link] Link003  label="holes_bottom"
  LinkedObject = -> <external ../U-fix.FCStd>#Sketch002
FEATURE [App::Link] Link004  label="bottom_fix_placement"
  LinkTransform = true
  LinkedObject = -> <external composit_stand3_base_part1_main.FCStd>#Placment003
FEATURE [Part::Extrusion] Extrude
  Base = -> Link003
  Dir = (0,0,1)
  DirMode = 2
  FaceMakerClass = Part::FaceMakerBullseye
  FaceMakerMode = 3
  LengthFwd = 20
  LengthRev = 0
  Solid = true
  Symmetric = false
FEATURE [Part::FeaturePython] Populate004  label="Populate PolarArray with bottom_fix_placement"  # WARN: FeaturePython — macro-defined, semantics opaque (R4)
  Copying = 0
  ExposePlacement = false
  MarkerShape = 1
  MarkerSize = 0
  NumElements = 3
  Object = -> Link004
  OutputCompounding = 0
  PlacementsTo = -> PolarArray
  Referencing = 1
  Type = lattice2PopulateCopies.LatticePopulateCopies
  isLattice = 1
FEATURE [Part::FeaturePython] Populate005  label="Populate Populate PolarArray with bottom_fix_placement with Extrude"  # WARN: FeaturePython — macro-defined, semantics opaque (R4)
  Copying = 0
  ExposePlacement = false
  MarkerShape = 1
  MarkerSize = 0
  NumElements = 0
  Object = -> Extrude
  OutputCompounding = 1
  PlacementsTo = -> Populate004
  Referencing = 0
  Type = lattice2PopulateCopies.LatticePopulateCopies
  isLattice = 0
FEATURE [App::Link] Link005  label="holes"
  LinkPlacement = pos=(0,0,0) rot=(0,0,1;3.14159rad)
  LinkedObject = -> <external composit_stand3_basin_holder_main.FCStd>#Join
  Placement = pos=(0,0,0) rot=(0,0,1;3.14159rad)
FEATURE [Part::Cylinder] Cylinder001  label="Cylinder"
  Angle = 360
  AttacherType = Attacher::AttachEngine3D
  FirstAngle = 0
  Height = 20
  Radius = 2.5
  SecondAngle = 0
FEATURE [Part::FeaturePython] Populate006  label="Populate holes with Cylinder"  # WARN: FeaturePython — macro-defined, semantics opaque (R4)
  Copying = 0
  ExposePlacement = false
  MarkerShape = 1
  MarkerSize = 0
  NumElements = 0
  Object = -> Cylinder001
  OutputCompounding = 1
  PlacementsTo = -> Link005
  Referencing = 0
  Type = lattice2PopulateCopies.LatticePopulateCopies
  isLattice = 0
FEATURE [Part::MultiFuse] Fusion
  Shapes = -> [Body001,Body002,Populate001,Populate005,Populate006]
FEATURE [PartDesign::Boolean] Boolean
  BaseFeature = -> Pad
  Group = -> [Fusion]
  Refine = true
  Suppressed = false
  Type = 1
  UsePlacement = true
FEATURE [PartDesign::Body] Body  label="top"
  AllowCompound = false
  Group = -> [Binder001,Pad,Boolean,Local_CS,Local_CS001,Local_CS002]
  Origin = -> Origin
  Tip = -> Boolean
---- part composit_stand3_basin_holder_model.FCStd = doc fcstd_3462062c95cc ----
FCSTD DOCUMENT  (FreeCAD 1.1R38827 (Git))
Label: composit_stand3_basin_holder_model
License: All rights reserved
LicenseURL: http://en.wikipedia.org/wiki/All_rights_reserved
objects: PartDesign::SubShapeBinder×2, Part::FeaturePython×2, Part::Mirroring×1, PartDesign::Pad×1, Part::Cylinder×1, App::Link×1, Part::MultiFuse×1, PartDesign::Boolean×1, PartDesign::CoordinateSystem×1, PartDesign::Body×1
note: 14 computed .brp shape members not serialized (recipe doc carries the construction recipe); baked Part::Feature solids carry a one-line shape summary decoded from their .brp
EXTERNAL_REF file=composit_stand3_basin_holder_main.FCStd obj=Sketch
EXTERNAL_REF file=composit_stand3_basin_holder_main.FCStd obj=Join

FEATURE [PartDesign::SubShapeBinder] Binder
  BindCopyOnChange = 0
  BindMode = 0
  ClaimChildren = true
  Fuse = false
  MakeFace = true
  OffsetFill = false
  OffsetIntersection = false
  OffsetJoinType = 0
  OffsetOpenResult = false
  PartialLoad = false
  Relative = false
  Support = -> [<external composit_stand3_basin_holder_main.FCStd>#Sketch]
  _Version = 2
FEATURE [Part::Mirroring] Part__Mirroring  label="Binder (Mirror #1)"
  Base = (0,0,0)
  Normal = (0,1,0)
  Source = -> Binder
FEATURE [Part::FeaturePython] Connect  # WARN: FeaturePython — macro-defined, semantics opaque (R4)
  Objects = -> [Binder,Part__Mirroring]
  Tolerance = 0
FEATURE [PartDesign::SubShapeBinder] Binder001
  BindCopyOnChange = 0
  BindMode = 0
  ClaimChildren = true
  Context = -> Body [Binder001.]
  Fuse = false
  MakeFace = true
  OffsetFill = false
  OffsetIntersection = false
  OffsetJoinType = 0
  OffsetOpenResult = false
  PartialLoad = false
  Relative = true
  Support = -> [Connect]
  _Version = 2
FEATURE [PartDesign::Pad] Pad
  Direction = (0,0,1)
  Length = 3
  Length2 = 10
  Profile = -> Binder001
  Suppressed = false
  Type = 0
FEATURE [Part::Cylinder] Cylinder
  Angle = 360
  AttacherType = Attacher::AttachEngine3D
  FirstAngle = 0
  Height = 10
  Radius = 1.7
  SecondAngle = 0
FEATURE [App::Link] Link  label="holes"
  LinkedObject = -> <external composit_stand3_basin_holder_main.FCStd>#Join
FEATURE [Part::FeaturePython] Populate  label="Populate holes with Cylinder"  # WARN: FeaturePython — macro-defined, semantics opaque (R4)
  Copying = 0
  ExposePlacement = false
  MarkerShape = 1
  MarkerSize = 0
  NumElements = 0
  Object = -> Cylinder
  OutputCompounding = 1
  PlacementsTo = -> Link
  Referencing = 0
  Type = lattice2PopulateCopies.LatticePopulateCopies
  isLattice = 0
FEATURE [Part::MultiFuse] Fusion
  Shapes = -> [Populate]
FEATURE [PartDesign::Boolean] Boolean
  BaseFeature = -> Pad
  Group = -> [Fusion]
  Suppressed = false
  Type = 1
  UsePlacement = true
FEATURE [PartDesign::CoordinateSystem] Local_CS
  AttacherType = Attacher::AttachEngine3D
  AttachmentSupport = -> [XY_Plane]
  MapMode = 5
FEATURE [PartDesign::Body] Body  label="basin_holder"
  AllowCompound = false
  Group = -> [Binder001,Pad,Boolean,Local_CS]
  Origin = -> Origin
  Tip = -> Boolean
